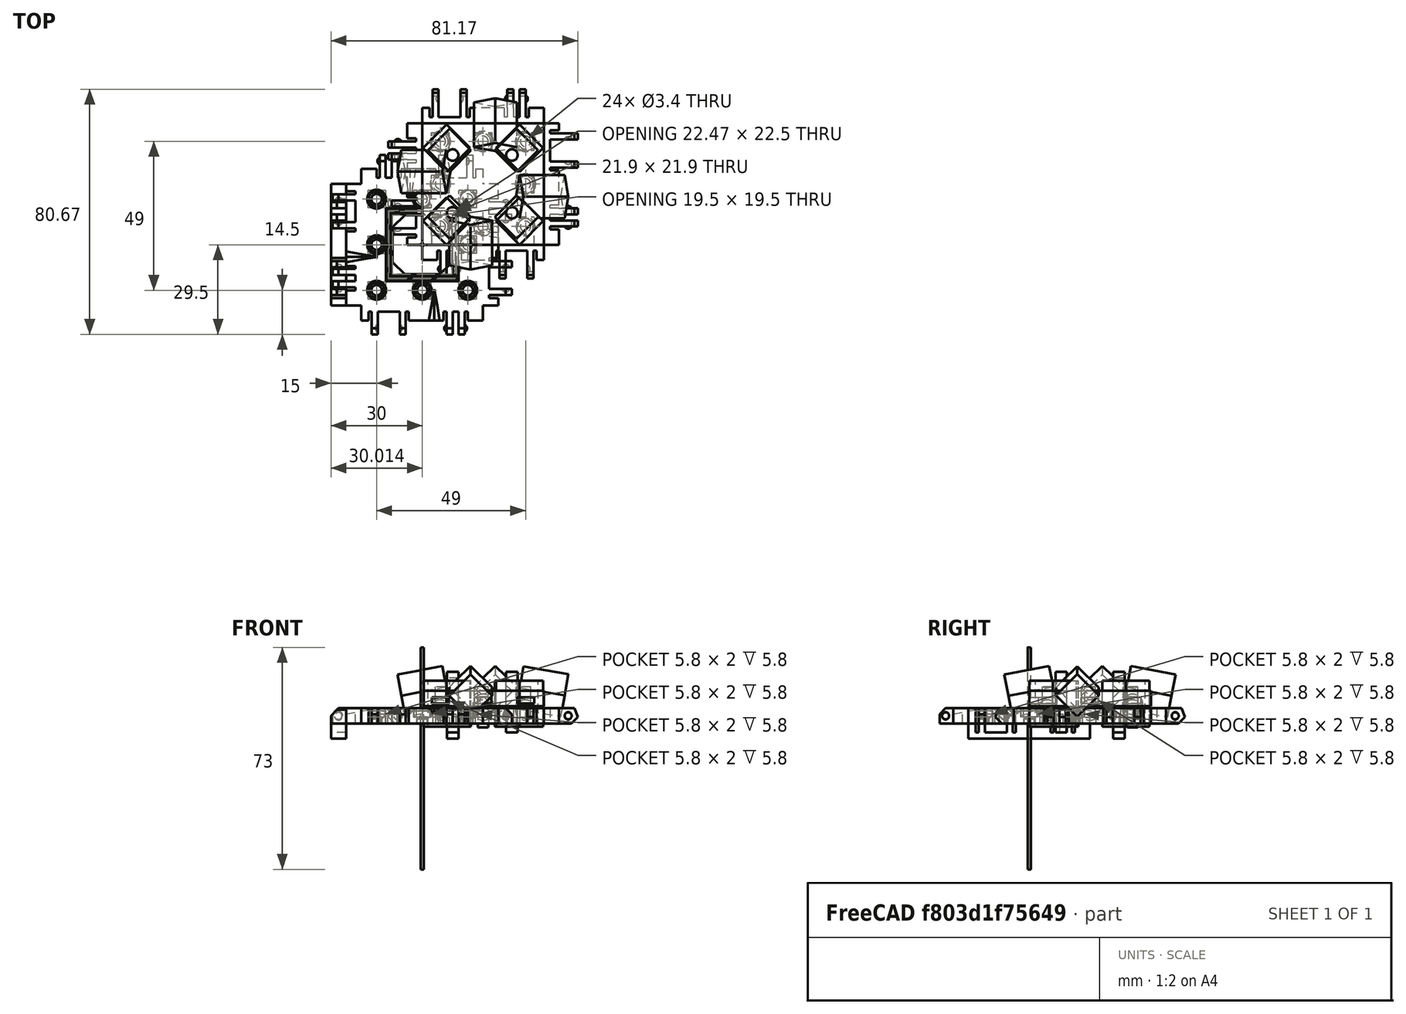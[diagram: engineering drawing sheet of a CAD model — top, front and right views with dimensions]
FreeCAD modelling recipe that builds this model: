
FCSTD DOCUMENT  (FreeCAD 0.17R13522 (Git))
Label: Robot Plates 1.2
License: All rights reserved
LicenseURL: http://en.wikipedia.org/wiki/All_rights_reserved
objects: Part::Box×265, Part::Cut×92, Part::Sphere×89, Part::MultiFuse×66, Part::Cylinder×42, Part::Fuse×30, Part::Chamfer×11, Drawing::FeatureViewAnnotation×10, App::DocumentObjectGroup×3, Part::Feature×3, Drawing::FeaturePage×2
note: 598 computed .brp shape members not serialized (recipe doc carries the construction recipe); baked Part::Feature solids carry a one-line shape summary decoded from their .brp

FEATURE [Part::Box] Box  label="Cube"
  AttacherType = Attacher::AttachEngine3D
  Height = 5
  Length = 40
  Placement = pos=(-20,-20,-2) rot=(0,0,1;0rad)
  Width = 40
FEATURE [Part::Sphere] Sphere003  label="Mag Hole 3"
  Angle1 = -90
  Angle2 = 90
  Angle3 = 360
  AttacherType = Attacher::AttachEngine3D
  Placement = pos=(-15,15,1.7) rot=(0,0,1;0rad)
  Radius = 2.83
FEATURE [Part::Sphere] Sphere005  label="Mag Hole 2"
  Angle1 = -90
  Angle2 = 90
  Angle3 = 360
  AttacherType = Attacher::AttachEngine3D
  Placement = pos=(15,0,1.7) rot=(0,0,1;0rad)
  Radius = 2.825
FEATURE [Part::Sphere] Sphere  label="Mag Hole"
  Angle1 = -90
  Angle2 = 90
  Angle3 = 360
  AttacherType = Attacher::AttachEngine3D
  Placement = pos=(-15,-15,1.7) rot=(0,0,1;0rad)
  Radius = 2.83
FEATURE [Part::MultiFuse] Fusion004  label="Ball Holes"
  Shapes = -> [Sphere,Sphere005,Sphere003]
FEATURE [Part::Cut] Cut003
  Base = -> Box
  Tool = -> Fusion004
FEATURE [Part::Box] Box001  label="Cube001"
  AttacherType = Attacher::AttachEngine3D
  Height = 7
  Length = 5
  Placement = pos=(-5,0,-2) rot=(0,0,1;0rad)
  Width = 40
FEATURE [Part::Box] Box002  label="Cube002"
  AttacherType = Attacher::AttachEngine3D
  Height = 7
  Length = 10
  Placement = pos=(-15,6,-2) rot=(0,0,1;0rad)
  Width = 2
FEATURE [Part::Box] Box003  label="Cube003"
  AttacherType = Attacher::AttachEngine3D
  Height = 7
  Length = 10
  Placement = pos=(-15,10,-2) rot=(0,0,1;0rad)
  Width = 2
FEATURE [Part::Box] Box004  label="Cube004"
  AttacherType = Attacher::AttachEngine3D
  Height = 7
  Length = 10
  Placement = pos=(-15,25.4,-2) rot=(0,0,1;0rad)
  Width = 2
FEATURE [Part::Box] Box005  label="Cube005"
  AttacherType = Attacher::AttachEngine3D
  Height = 7
  Length = 10
  Placement = pos=(-15,34.6,-2) rot=(0,0,1;0rad)
  Width = 2
FEATURE [Part::Sphere] Sphere008
  Angle1 = -90
  Angle2 = 90
  Angle3 = 360
  AttacherType = Attacher::AttachEngine3D
  Placement = pos=(-7.5,6.5,0.5) rot=(0,0,1;0rad)
  Radius = 1.25
FEATURE [Part::Box] Box006  label="Chamfer Cube"
  AttacherType = Attacher::AttachEngine3D
  Height = 10
  Length = 13
  Placement = pos=(-11.69,0,-1.19) rot=(0,-1,0;0.785398rad)
  Width = 40
FEATURE [Part::Sphere] Sphere009
  Angle1 = -90
  Angle2 = 90
  Angle3 = 360
  AttacherType = Attacher::AttachEngine3D
  Placement = pos=(-7.5,11.5,0.5) rot=(0,0,1;0rad)
  Radius = 1.25
FEATURE [Part::Sphere] Sphere010
  Angle1 = -90
  Angle2 = 90
  Angle3 = 360
  AttacherType = Attacher::AttachEngine3D
  Placement = pos=(-7.5,28,0.5) rot=(0,0,1;0rad)
  Radius = 1.5
FEATURE [Part::Sphere] Sphere011
  Angle1 = -90
  Angle2 = 90
  Angle3 = 360
  AttacherType = Attacher::AttachEngine3D
  Placement = pos=(-7.5,34,0.5) rot=(0,0,1;0rad)
  Radius = 1.5
FEATURE [Part::Box] Box007  label="Cube007"
  AttacherType = Attacher::AttachEngine3D
  Height = 7
  Length = 4
  Placement = pos=(-6,5,-2) rot=(0,0,1;0rad)
  Width = 1
FEATURE [Part::Box] Box008  label="Cube008"
  AttacherType = Attacher::AttachEngine3D
  Height = 7
  Length = 4
  Placement = pos=(-6,8,-2) rot=(0,0,1;0rad)
  Width = 2
FEATURE [Part::Box] Box009  label="Cube009"
  AttacherType = Attacher::AttachEngine3D
  Height = 7
  Length = 4
  Placement = pos=(-6,12,-2) rot=(0,0,1;0rad)
  Width = 1
FEATURE [Part::Box] Box010  label="Cube010"
  AttacherType = Attacher::AttachEngine3D
  Height = 7
  Length = 4
  Placement = pos=(-6,24.4,-2) rot=(0,0,1;0rad)
  Width = 1
FEATURE [Part::Box] Box011  label="Cube011"
  AttacherType = Attacher::AttachEngine3D
  Height = 7
  Length = 4
  Placement = pos=(-6,36.6,-2) rot=(0,0,1;0rad)
  Width = 1
FEATURE [Part::Box] Box012  label="Cube012"
  AttacherType = Attacher::AttachEngine3D
  Height = 7
  Length = 4
  Placement = pos=(-6,27.4,-2) rot=(0,0,1;0rad)
  Width = 7.2
FEATURE [Part::MultiFuse] Fusion003  label="Extra Holes for Clips"
  Shapes = -> [Box012,Box009,Box011,Box008,Box010,Box007]
FEATURE [Part::Box] Box013  label="Re-level Edge Clip Block"
  AttacherType = Attacher::AttachEngine3D
  Height = 10
  Length = 20
  Placement = pos=(-19,-2,3) rot=(0,0,1;0rad)
  Width = 44
FEATURE [Part::Box] Box014  label="Cube014"
  AttacherType = Attacher::AttachEngine3D
  Height = 7
  Length = 10
  Placement = pos=(-10,34.6,0) rot=(0,0,1;0rad)
  Width = 2
FEATURE [Part::Box] Box015  label="Cube015"
  AttacherType = Attacher::AttachEngine3D
  Height = 7
  Length = 5
  Width = 40
FEATURE [Part::Box] Box016  label="Cube016"
  AttacherType = Attacher::AttachEngine3D
  Height = 7
  Length = 10
  Placement = pos=(-10,25.4,0) rot=(0,0,1;0rad)
  Width = 2
FEATURE [Part::Box] Box017  label="Cube017"
  AttacherType = Attacher::AttachEngine3D
  Height = 7
  Length = 10
  Placement = pos=(-10,10,0) rot=(0,0,1;0rad)
  Width = 2
FEATURE [Part::Box] Box018  label="Cube018"
  AttacherType = Attacher::AttachEngine3D
  Height = 7
  Length = 10
  Placement = pos=(-10,6,0) rot=(0,0,1;0rad)
  Width = 2
FEATURE [Part::Sphere] Sphere012
  Angle1 = -90
  Angle2 = 90
  Angle3 = 360
  AttacherType = Attacher::AttachEngine3D
  Placement = pos=(-3,6.5,2.5) rot=(0,0,1;0rad)
  Radius = 1.25
FEATURE [Part::Box] Box019  label="Cube019"
  AttacherType = Attacher::AttachEngine3D
  Height = 10
  Length = 13
  Placement = pos=(-10.19,0,-1.19) rot=(0,-1,0;0.785398rad)
  Width = 40
FEATURE [Part::Sphere] Sphere013
  Angle1 = -90
  Angle2 = 90
  Angle3 = 360
  AttacherType = Attacher::AttachEngine3D
  Placement = pos=(-3,11.5,2.5) rot=(0,0,1;0rad)
  Radius = 1.25
FEATURE [Part::Sphere] Sphere014
  Angle1 = -90
  Angle2 = 90
  Angle3 = 360
  AttacherType = Attacher::AttachEngine3D
  Placement = pos=(-3,28,2.5) rot=(0,0,1;0rad)
  Radius = 1.5
FEATURE [Part::Sphere] Sphere015
  Angle1 = -90
  Angle2 = 90
  Angle3 = 360
  AttacherType = Attacher::AttachEngine3D
  Placement = pos=(-3,34,2.5) rot=(0,0,1;0rad)
  Radius = 1.5
FEATURE [Part::MultiFuse] Fusion005
  Shapes = -> [Box015,Box018,Box017,Box016,Box014]
FEATURE [Part::Cut] Cut005
  Base = -> Fusion005
  Tool = -> Box019
FEATURE [Part::MultiFuse] Fusion006
  Shapes = -> [Sphere012,Sphere013,Cut005]
FEATURE [Part::MultiFuse] Fusion007
  Shapes = -> [Sphere015,Sphere014]
FEATURE [Part::Cut] Cut006
  Base = -> Fusion006
  Tool = -> Fusion007
FEATURE [Part::Chamfer] Chamfer002
  Base = -> Cut006
  Edges = 4 edges r=4: [Edge31,Edge37,Edge43,Edge46]
FEATURE [Part::Box] Box020  label="Cube020"
  AttacherType = Attacher::AttachEngine3D
  Height = 7
  Length = 4
  Placement = pos=(-1,5,0) rot=(0,0,1;0rad)
  Width = 1
FEATURE [Part::Box] Box021  label="Cube021"
  AttacherType = Attacher::AttachEngine3D
  Height = 7
  Length = 4
  Placement = pos=(-1,8,0) rot=(0,0,1;0rad)
  Width = 2
FEATURE [Part::Box] Box022  label="Cube022"
  AttacherType = Attacher::AttachEngine3D
  Height = 7
  Length = 4
  Placement = pos=(-1,12,0) rot=(0,0,1;0rad)
  Width = 1
FEATURE [Part::Box] Box023  label="Cube023"
  AttacherType = Attacher::AttachEngine3D
  Height = 7
  Length = 4
  Placement = pos=(-1,24.4,0) rot=(0,0,1;0rad)
  Width = 1
FEATURE [Part::Box] Box024  label="Cube024"
  AttacherType = Attacher::AttachEngine3D
  Height = 7
  Length = 4
  Placement = pos=(-1,36.6,0) rot=(0,0,1;0rad)
  Width = 1
FEATURE [Part::Box] Box025  label="Cube025"
  AttacherType = Attacher::AttachEngine3D
  Height = 7
  Length = 4
  Placement = pos=(-1,27.4,0) rot=(0,0,1;0rad)
  Width = 7.2
FEATURE [Part::MultiFuse] Fusion008
  Shapes = -> [Box025,Box022,Box024,Box021,Box023,Box020]
FEATURE [Part::Cut] Cut007
  Base = -> Chamfer002
  Placement = pos=(-5,40,3) rot=(1,0,0;3.14159rad)
  Tool = -> Fusion008
FEATURE [Part::Box] Box026  label="Cube026"
  AttacherType = Attacher::AttachEngine3D
  Height = 10
  Length = 12
  Placement = pos=(-11,-2,-12) rot=(0,0,1;0rad)
  Width = 44
FEATURE [Part::Cut] Cut008
  Base = -> Cut007
  Placement = pos=(40,0,0) rot=(0,0,1;1.5708rad)
  Tool = -> Box026
FEATURE [Part::Box] Box027  label="Cube027"
  AttacherType = Attacher::AttachEngine3D
  Height = 7
  Length = 4
  Placement = pos=(-1,12,0) rot=(0,0,1;0rad)
  Width = 1
FEATURE [Part::Box] Box028  label="Cube028"
  AttacherType = Attacher::AttachEngine3D
  Height = 10
  Length = 13
  Placement = pos=(-10.19,0,-1.19) rot=(0,-1,0;0.785398rad)
  Width = 40
FEATURE [Part::Box] Box029  label="Cube029"
  AttacherType = Attacher::AttachEngine3D
  Height = 7
  Length = 4
  Placement = pos=(-1,27.4,0) rot=(0,0,1;0rad)
  Width = 7.2
FEATURE [Part::Box] Box030  label="Cube030"
  AttacherType = Attacher::AttachEngine3D
  Height = 7
  Length = 4
  Placement = pos=(-1,5,0) rot=(0,0,1;0rad)
  Width = 1
FEATURE [Part::Box] Box031  label="Cube031"
  AttacherType = Attacher::AttachEngine3D
  Height = 7
  Length = 10
  Placement = pos=(-10,6,0) rot=(0,0,1;0rad)
  Width = 2
FEATURE [Part::Box] Box032  label="Cube032"
  AttacherType = Attacher::AttachEngine3D
  Height = 10
  Length = 12
  Placement = pos=(-11,-2,-12) rot=(0,0,1;0rad)
  Width = 44
FEATURE [Part::Sphere] Sphere016
  Angle1 = -90
  Angle2 = 90
  Angle3 = 360
  AttacherType = Attacher::AttachEngine3D
  Placement = pos=(-3,6.5,2.5) rot=(0,0,1;0rad)
  Radius = 1.25
FEATURE [Part::Box] Box033  label="Cube033"
  AttacherType = Attacher::AttachEngine3D
  Height = 7
  Length = 10
  Placement = pos=(-10,25.4,0) rot=(0,0,1;0rad)
  Width = 2
FEATURE [Part::Box] Box034  label="Cube034"
  AttacherType = Attacher::AttachEngine3D
  Height = 7
  Length = 10
  Placement = pos=(-10,10,0) rot=(0,0,1;0rad)
  Width = 2
FEATURE [Part::Sphere] Sphere017
  Angle1 = -90
  Angle2 = 90
  Angle3 = 360
  AttacherType = Attacher::AttachEngine3D
  Placement = pos=(-3,28,2.5) rot=(0,0,1;0rad)
  Radius = 1.5
FEATURE [Part::Sphere] Sphere018
  Angle1 = -90
  Angle2 = 90
  Angle3 = 360
  AttacherType = Attacher::AttachEngine3D
  Placement = pos=(-3,11.5,2.5) rot=(0,0,1;0rad)
  Radius = 1.25
FEATURE [Part::Box] Box035  label="Cube035"
  AttacherType = Attacher::AttachEngine3D
  Height = 7
  Length = 4
  Placement = pos=(-1,36.6,0) rot=(0,0,1;0rad)
  Width = 1
FEATURE [Part::Sphere] Sphere019
  Angle1 = -90
  Angle2 = 90
  Angle3 = 360
  AttacherType = Attacher::AttachEngine3D
  Placement = pos=(-3,34,2.5) rot=(0,0,1;0rad)
  Radius = 1.5
FEATURE [Part::MultiFuse] Fusion011
  Shapes = -> [Sphere019,Sphere017]
FEATURE [Part::Box] Box036  label="Cube036"
  AttacherType = Attacher::AttachEngine3D
  Height = 7
  Length = 4
  Placement = pos=(-1,8,0) rot=(0,0,1;0rad)
  Width = 2
FEATURE [Part::Box] Box037  label="Cube037"
  AttacherType = Attacher::AttachEngine3D
  Height = 7
  Length = 10
  Placement = pos=(-10,34.6,0) rot=(0,0,1;0rad)
  Width = 2
FEATURE [Part::Box] Box038  label="Cube038"
  AttacherType = Attacher::AttachEngine3D
  Height = 7
  Length = 4
  Placement = pos=(-1,24.4,0) rot=(0,0,1;0rad)
  Width = 1
FEATURE [Part::MultiFuse] Fusion009
  Shapes = -> [Box029,Box027,Box035,Box036,Box038,Box030]
FEATURE [Part::Box] Box039  label="Cube039"
  AttacherType = Attacher::AttachEngine3D
  Height = 7
  Length = 5
  Width = 40
FEATURE [Part::MultiFuse] Fusion012
  Shapes = -> [Box039,Box031,Box034,Box033,Box037]
FEATURE [Part::Cut] Cut011
  Base = -> Fusion012
  Tool = -> Box028
FEATURE [Part::MultiFuse] Fusion010
  Shapes = -> [Sphere016,Sphere018,Cut011]
FEATURE [Part::Cut] Cut012
  Base = -> Fusion010
  Tool = -> Fusion011
FEATURE [Part::Chamfer] Chamfer003
  Base = -> Cut012
  Edges = 4 edges r=4: [Edge31,Edge37,Edge43,Edge46]
FEATURE [Part::Cut] Cut010
  Base = -> Chamfer003
  Placement = pos=(-5,40,3) rot=(1,0,0;3.14159rad)
  Tool = -> Fusion009
FEATURE [Part::Cut] Cut009
  Base = -> Cut010
  Placement = pos=(40,40,0) rot=(0,0,1;3.14159rad)
  Tool = -> Box032
FEATURE [Part::Sphere] Sphere020
  Angle1 = -90
  Angle2 = 90
  Angle3 = 360
  AttacherType = Attacher::AttachEngine3D
  Placement = pos=(-3,11.5,2.5) rot=(0,0,1;0rad)
  Radius = 1.25
FEATURE [Part::Box] Box040  label="Cube040"
  AttacherType = Attacher::AttachEngine3D
  Height = 7
  Length = 10
  Placement = pos=(-10,6,0) rot=(0,0,1;0rad)
  Width = 2
FEATURE [Part::Box] Box041  label="Cube041"
  AttacherType = Attacher::AttachEngine3D
  Height = 7
  Length = 4
  Placement = pos=(-1,8,0) rot=(0,0,1;0rad)
  Width = 2
FEATURE [Part::Box] Box042  label="Cube042"
  AttacherType = Attacher::AttachEngine3D
  Height = 7
  Length = 10
  Placement = pos=(-10,10,0) rot=(0,0,1;0rad)
  Width = 2
FEATURE [Part::Box] Box043  label="Cube043"
  AttacherType = Attacher::AttachEngine3D
  Height = 10
  Length = 12
  Placement = pos=(-11,-2,-12) rot=(0,0,1;0rad)
  Width = 44
FEATURE [Part::Box] Box044  label="Cube044"
  AttacherType = Attacher::AttachEngine3D
  Height = 7
  Length = 4
  Placement = pos=(-1,5,0) rot=(0,0,1;0rad)
  Width = 1
FEATURE [Part::Sphere] Sphere021
  Angle1 = -90
  Angle2 = 90
  Angle3 = 360
  AttacherType = Attacher::AttachEngine3D
  Placement = pos=(-3,28,2.5) rot=(0,0,1;0rad)
  Radius = 1.5
FEATURE [Part::Sphere] Sphere022
  Angle1 = -90
  Angle2 = 90
  Angle3 = 360
  AttacherType = Attacher::AttachEngine3D
  Placement = pos=(-3,6.5,2.5) rot=(0,0,1;0rad)
  Radius = 1.25
FEATURE [Part::Sphere] Sphere023
  Angle1 = -90
  Angle2 = 90
  Angle3 = 360
  AttacherType = Attacher::AttachEngine3D
  Placement = pos=(-3,34,2.5) rot=(0,0,1;0rad)
  Radius = 1.5
FEATURE [Part::Box] Box045  label="Cube045"
  AttacherType = Attacher::AttachEngine3D
  Height = 7
  Length = 4
  Placement = pos=(-1,12,0) rot=(0,0,1;0rad)
  Width = 1
FEATURE [Part::Box] Box046  label="Cube046"
  AttacherType = Attacher::AttachEngine3D
  Height = 7
  Length = 5
  Width = 40
FEATURE [Part::Box] Box047  label="Cube047"
  AttacherType = Attacher::AttachEngine3D
  Height = 7
  Length = 4
  Placement = pos=(-1,36.6,0) rot=(0,0,1;0rad)
  Width = 1
FEATURE [Part::Box] Box048  label="Cube048"
  AttacherType = Attacher::AttachEngine3D
  Height = 7
  Length = 4
  Placement = pos=(-1,24.4,0) rot=(0,0,1;0rad)
  Width = 1
FEATURE [Part::Box] Box049  label="Cube049"
  AttacherType = Attacher::AttachEngine3D
  Height = 7
  Length = 10
  Placement = pos=(-10,25.4,0) rot=(0,0,1;0rad)
  Width = 2
FEATURE [Part::Box] Box050  label="Cube050"
  AttacherType = Attacher::AttachEngine3D
  Height = 10
  Length = 13
  Placement = pos=(-10.19,0,-1.19) rot=(0,-1,0;0.785398rad)
  Width = 40
FEATURE [Part::Box] Box051  label="Cube051"
  AttacherType = Attacher::AttachEngine3D
  Height = 7
  Length = 10
  Placement = pos=(-10,34.6,0) rot=(0,0,1;0rad)
  Width = 2
FEATURE [Part::MultiFuse] Fusion015
  Shapes = -> [Box046,Box040,Box042,Box049,Box051]
FEATURE [Part::Cut] Cut013
  Base = -> Fusion015
  Tool = -> Box050
FEATURE [Part::MultiFuse] Fusion013
  Shapes = -> [Sphere022,Sphere020,Cut013]
FEATURE [Part::MultiFuse] Fusion016
  Shapes = -> [Sphere023,Sphere021]
FEATURE [Part::Cut] Cut014
  Base = -> Fusion013
  Tool = -> Fusion016
FEATURE [Part::Chamfer] Chamfer004
  Base = -> Cut014
  Edges = 4 edges r=4: [Edge31,Edge37,Edge43,Edge46]
FEATURE [Part::Box] Box052  label="Cube052"
  AttacherType = Attacher::AttachEngine3D
  Height = 7
  Length = 4
  Placement = pos=(-1,27.4,0) rot=(0,0,1;0rad)
  Width = 7.2
FEATURE [Part::MultiFuse] Fusion014
  Shapes = -> [Box052,Box045,Box047,Box041,Box048,Box044]
FEATURE [Part::Cut] Cut016
  Base = -> Chamfer004
  Placement = pos=(-5,40,3) rot=(1,0,0;3.14159rad)
  Tool = -> Fusion014
FEATURE [Part::Cut] Cut015
  Base = -> Cut016
  Placement = pos=(0,40,0) rot=(0,0,-1;1.5708rad)
  Tool = -> Box043
FEATURE [Part::Box] Box054  label="Cube054"
  AttacherType = Attacher::AttachEngine3D
  Height = 15
  Length = 10
  Placement = pos=(9,2,-3) rot=(0,0,1;0.785398rad)
  Width = 10
FEATURE [Part::Box] Box055  label="Cube055"
  AttacherType = Attacher::AttachEngine3D
  Height = 15
  Length = 10
  Placement = pos=(31,24,-3) rot=(0,0,1;0.785398rad)
  Width = 10
FEATURE [Part::Box] Box056  label="Cube056"
  AttacherType = Attacher::AttachEngine3D
  Height = 15
  Length = 10
  Placement = pos=(31,2,-3) rot=(0,0,1;0.785398rad)
  Width = 10
FEATURE [Part::Box] Box057  label="Cube057"
  AttacherType = Attacher::AttachEngine3D
  Height = 15
  Length = 10
  Placement = pos=(9,24,-3) rot=(0,0,1;0.785398rad)
  Width = 10
FEATURE [Part::MultiFuse] Fusion017
  Shapes = -> [Box054,Box057,Box056,Box055]
FEATURE [Part::Box] Box058  label="Cube058"
  AttacherType = Attacher::AttachEngine3D
  Height = 5
  Length = 40
  Placement = pos=(0,0,3.7) rot=(0,0,1;0rad)
  Width = 40
FEATURE [Part::Box] Box059  label="Square Nut Hole 008"
  AttacherType = Attacher::AttachEngine3D
  Height = 2
  Length = 5.6
  Placement = pos=(17.2,31.2,4.6) rot=(0,0,1;0rad)
  Width = 5.6
FEATURE [Part::Box] Box060  label="Square Nut Hole 009"
  AttacherType = Attacher::AttachEngine3D
  Height = 2
  Length = 5.6
  Placement = pos=(17.2,-0.85,4.6) rot=(0,0,1;0rad)
  Width = 10
FEATURE [Part::Box] Box061  label="Square Nut Hole 010"
  AttacherType = Attacher::AttachEngine3D
  Height = 2
  Length = 5.6
  Placement = pos=(31.2,-0.85,4.6) rot=(0,0,1;0rad)
  Width = 10
FEATURE [Part::Box] Box062  label="Square Nut Hole 011"
  AttacherType = Attacher::AttachEngine3D
  Height = 2
  Length = 5.4
  Placement = pos=(31.3,17.3,4.6) rot=(0,0,1;0rad)
  Width = 5.4
FEATURE [Part::Box] Box063  label="Square Nut Hole 012"
  AttacherType = Attacher::AttachEngine3D
  Height = 2
  Length = 5.7
  Placement = pos=(3.15,31.15,4.6) rot=(0,0,1;0rad)
  Width = 5.7
FEATURE [Part::Box] Box064  label="Square Nut Hole 013"
  AttacherType = Attacher::AttachEngine3D
  Height = 2
  Length = 5.5
  Placement = pos=(31.25,31.25,4.6) rot=(0,0,1;0rad)
  Width = 5.5
FEATURE [Part::Box] Box065  label="Square Nut Hole 014"
  AttacherType = Attacher::AttachEngine3D
  Height = 2
  Length = 5.8
  Placement = pos=(3.1,17.1,4.6) rot=(0,0,1;0rad)
  Width = 5.8
FEATURE [Part::Box] Box066  label="Square Nut Hole 015"
  AttacherType = Attacher::AttachEngine3D
  Height = 2
  Length = 5.6
  Placement = pos=(3.2,-0.85,4.6) rot=(0,0,1;0rad)
  Width = 10
FEATURE [Part::Sphere] Sphere006  label="Nut Clearence1"
  Angle1 = -90
  Angle2 = 90
  Angle3 = 360
  AttacherType = Attacher::AttachEngine3D
  Placement = pos=(6,6,2.4) rot=(0,0,1;0rad)
  Radius = 3.35
FEATURE [Part::Sphere] Sphere024
  Angle1 = -90
  Angle2 = 90
  Angle3 = 360
  AttacherType = Attacher::AttachEngine3D
  Placement = pos=(6,34,2.4) rot=(0,0,1;0rad)
  Radius = 3.35
FEATURE [Part::Sphere] Sphere007
  Angle1 = -90
  Angle2 = 90
  Angle3 = 360
  AttacherType = Attacher::AttachEngine3D
  Placement = pos=(34,20,2.4) rot=(0,0,1;0rad)
  Radius = 3.35
FEATURE [Part::Sphere] Sphere001
  Angle1 = -90
  Angle2 = 90
  Angle3 = 360
  AttacherType = Attacher::AttachEngine3D
  Placement = pos=(34,6,2.4) rot=(0,0,1;0rad)
  Radius = 3.35
FEATURE [Part::Sphere] Sphere025
  Angle1 = -90
  Angle2 = 90
  Angle3 = 360
  AttacherType = Attacher::AttachEngine3D
  Placement = pos=(20,6,2.4) rot=(0,0,1;0rad)
  Radius = 3.35
FEATURE [Part::Sphere] Sphere026
  Angle1 = -90
  Angle2 = 90
  Angle3 = 360
  AttacherType = Attacher::AttachEngine3D
  Placement = pos=(20,34,2.4) rot=(0,0,1;0rad)
  Radius = 3.35
FEATURE [Part::Sphere] Sphere004
  Angle1 = -90
  Angle2 = 90
  Angle3 = 360
  AttacherType = Attacher::AttachEngine3D
  Placement = pos=(6,20,2.4) rot=(0,0,1;0rad)
  Radius = 3.35
FEATURE [Part::Sphere] Sphere002
  Angle1 = -90
  Angle2 = 90
  Angle3 = 360
  AttacherType = Attacher::AttachEngine3D
  Placement = pos=(34,34,2.4) rot=(0,0,1;0rad)
  Radius = 3.35
FEATURE [Part::Cylinder] Cylinder
  Angle = 360
  AttacherType = Attacher::AttachEngine3D
  Height = 10
  Placement = pos=(6,6,0) rot=(0,0,1;0rad)
  Radius = 1.7
FEATURE [Part::Cylinder] Cylinder002
  Angle = 360
  AttacherType = Attacher::AttachEngine3D
  Height = 10
  Placement = pos=(34,6,0) rot=(0,0,1;0rad)
  Radius = 1.7
FEATURE [Part::Cylinder] Cylinder001
  Angle = 360
  AttacherType = Attacher::AttachEngine3D
  Height = 10
  Placement = pos=(20,6,0) rot=(0,0,1;0rad)
  Radius = 1.7
FEATURE [Part::Cylinder] Cylinder003
  Angle = 360
  AttacherType = Attacher::AttachEngine3D
  Height = 10
  Placement = pos=(34,34,0) rot=(0,0,1;0rad)
  Radius = 1.7
FEATURE [Part::Cylinder] Cylinder004
  Angle = 360
  AttacherType = Attacher::AttachEngine3D
  Height = 10
  Placement = pos=(20,34,0) rot=(0,0,1;0rad)
  Radius = 1.7
FEATURE [Part::Cylinder] Cylinder005
  Angle = 360
  AttacherType = Attacher::AttachEngine3D
  Height = 10
  Placement = pos=(6,34,0) rot=(0,0,1;0rad)
  Radius = 1.7
FEATURE [Part::Cylinder] Cylinder006
  Angle = 360
  AttacherType = Attacher::AttachEngine3D
  Height = 10
  Placement = pos=(6,20,0) rot=(0,0,1;0rad)
  Radius = 1.7
FEATURE [Part::Cylinder] Cylinder007
  Angle = 360
  AttacherType = Attacher::AttachEngine3D
  Height = 10
  Placement = pos=(34,20,0) rot=(0,0,1;0rad)
  Radius = 1.7
FEATURE [Part::MultiFuse] Fusion018
  Shapes = -> [Cylinder,Cylinder004,Cylinder007,Cylinder005,Cylinder006,Cylinder001,Cylinder002,Cylinder003]
FEATURE [Part::MultiFuse] Fusion019
  Shapes = -> [Sphere007,Sphere024,Sphere006,Sphere025,Sphere001,Sphere026,Sphere004,Sphere002]
FEATURE [Part::MultiFuse] Fusion020
  Shapes = -> [Box061,Box065,Box062,Box063,Box064,Box066,Box059,Box060]
FEATURE [Part::Cut] Cut017
  Base = -> Box058
  Tool = -> Fusion020
FEATURE [Part::Cut] Cut019
  Base = -> Cut017
  Tool = -> Fusion019
FEATURE [Part::Cut] Cut018
  Base = -> Cut019
  Tool = -> Fusion018
FEATURE [Part::Cylinder] Cylinder008
  Angle = 360
  AttacherType = Attacher::AttachEngine3D
  Height = 20
  Placement = pos=(10,10.5,-5) rot=(0,0,1;0rad)
  Radius = 1.9
FEATURE [Part::Cylinder] Cylinder009
  Angle = 360
  AttacherType = Attacher::AttachEngine3D
  Height = 20
  Placement = pos=(29.5,10.5,-5) rot=(0,0,1;0rad)
  Radius = 1.9
FEATURE [Part::Cylinder] Cylinder010
  Angle = 360
  AttacherType = Attacher::AttachEngine3D
  Height = 20
  Placement = pos=(29.5,29.5,-5) rot=(0,0,1;0rad)
  Radius = 1.9
FEATURE [Part::Cylinder] Cylinder011
  Angle = 360
  AttacherType = Attacher::AttachEngine3D
  Height = 20
  Placement = pos=(10,29.5,-7) rot=(0,0,1;0rad)
  Radius = 1.9
FEATURE [Part::MultiFuse] Fusion021  label="M2 Screw holes"
  Shapes = -> [Cylinder008,Cylinder009,Cylinder011,Cylinder010]
FEATURE [Part::Box] Box067  label="Square Nut Hole 016"
  AttacherType = Attacher::AttachEngine3D
  Height = 2
  Length = 5.8
  Placement = pos=(31.1,17.1,4.6) rot=(0,0,1;0rad)
  Width = 5.8
FEATURE [Part::Box] Box068  label="Square Nut Hole 017"
  AttacherType = Attacher::AttachEngine3D
  Height = 2
  Length = 5.8
  Placement = pos=(17.1,36.9,2.1) rot=(1,0,0;3.14159rad)
  Width = 5.8
FEATURE [Part::Box] Box069  label="Square Nut Hole 018"
  AttacherType = Attacher::AttachEngine3D
  Height = 2
  Length = 5.8
  Placement = pos=(-2.9,2.9,2.1) rot=(1,0,0;3.14159rad)
  Width = 5.8
FEATURE [Part::Box] Box070  label="Square Nut Hole 019"
  AttacherType = Attacher::AttachEngine3D
  Height = 2
  Length = 5.8
  Placement = pos=(3.1,3.1,4.6) rot=(0,0,1;0rad)
  Width = 5.8
FEATURE [Part::Box] Box071  label="Square Nut Hole 020"
  AttacherType = Attacher::AttachEngine3D
  Height = 2
  Length = 5.8
  Placement = pos=(3.1,31.1,4.6) rot=(0,0,1;0rad)
  Width = 5.8
FEATURE [Part::Box] Box072  label="Square Nut Hole 021"
  AttacherType = Attacher::AttachEngine3D
  Height = 2
  Length = 5.8
  Placement = pos=(17.1,31.1,4.6) rot=(0,0,1;0rad)
  Width = 5.8
FEATURE [Part::Box] Box073  label="Square Nut Hole 022"
  AttacherType = Attacher::AttachEngine3D
  Height = 2
  Length = 5.8
  Placement = pos=(31.1,31.1,4.6) rot=(0,0,1;0rad)
  Width = 5.8
FEATURE [Part::Box] Box074  label="Square Nut Hole 023"
  AttacherType = Attacher::AttachEngine3D
  Height = 2
  Length = 5.8
  Placement = pos=(3.1,17.1,4.6) rot=(0,0,1;0rad)
  Width = 5.8
FEATURE [Part::Cylinder] Cylinder012
  Angle = 360
  AttacherType = Attacher::AttachEngine3D
  Height = 10
  Placement = pos=(6,6,0) rot=(0,0,1;0rad)
  Radius = 1.7
FEATURE [Part::Cylinder] Cylinder013
  Angle = 360
  AttacherType = Attacher::AttachEngine3D
  Height = 10
  Placement = pos=(34,34,0) rot=(0,0,1;0rad)
  Radius = 1.7
FEATURE [Part::Cylinder] Cylinder014
  Angle = 360
  AttacherType = Attacher::AttachEngine3D
  Height = 10
  Placement = pos=(20,34,0) rot=(0,0,1;0rad)
  Radius = 1.7
FEATURE [Part::Cylinder] Cylinder015
  Angle = 360
  AttacherType = Attacher::AttachEngine3D
  Height = 10
  Placement = pos=(6,34,0) rot=(0,0,1;0rad)
  Radius = 1.7
FEATURE [Part::Cylinder] Cylinder016
  Angle = 360
  AttacherType = Attacher::AttachEngine3D
  Height = 10
  Placement = pos=(6,20,0) rot=(0,0,1;0rad)
  Radius = 1.7
FEATURE [Part::Cylinder] Cylinder017
  Angle = 360
  AttacherType = Attacher::AttachEngine3D
  Height = 10
  Placement = pos=(34,20,0) rot=(0,0,1;0rad)
  Radius = 1.7
FEATURE [Part::Cylinder] Cylinder018
  Angle = 360
  AttacherType = Attacher::AttachEngine3D
  Height = 10
  Placement = pos=(0,0,6.7) rot=(1,0,0;3.14159rad)
  Radius = 1.7
FEATURE [Part::Cylinder] Cylinder019
  Angle = 360
  AttacherType = Attacher::AttachEngine3D
  Height = 10
  Placement = pos=(20,34,6.7) rot=(1,0,0;3.14159rad)
  Radius = 1.7
FEATURE [Part::Box] Box075  label="Cube059"
  AttacherType = Attacher::AttachEngine3D
  Height = 5
  Length = 40
  Placement = pos=(-20,-20,-2) rot=(0,0,1;0rad)
  Width = 40
FEATURE [Part::Sphere] Sphere027
  Angle1 = -90
  Angle2 = 90
  Angle3 = 360
  AttacherType = Attacher::AttachEngine3D
  Placement = pos=(34,20,2.4) rot=(0,0,1;0rad)
  Radius = 3.35
FEATURE [Part::Sphere] Sphere028  label="Nut Clearence002"
  Angle1 = -90
  Angle2 = 90
  Angle3 = 360
  AttacherType = Attacher::AttachEngine3D
  Placement = pos=(6,6,2.4) rot=(0,0,1;0rad)
  Radius = 3.35
FEATURE [Part::Sphere] Sphere029
  Angle1 = -90
  Angle2 = 90
  Angle3 = 360
  AttacherType = Attacher::AttachEngine3D
  Placement = pos=(34,34,2.4) rot=(0,0,1;0rad)
  Radius = 3.35
FEATURE [Part::Sphere] Sphere030
  Angle1 = -90
  Angle2 = 90
  Angle3 = 360
  AttacherType = Attacher::AttachEngine3D
  Placement = pos=(0,0,4.3) rot=(1,0,0;3.14159rad)
  Radius = 3.35
FEATURE [Part::Sphere] Sphere031
  Angle1 = -90
  Angle2 = 90
  Angle3 = 360
  AttacherType = Attacher::AttachEngine3D
  Placement = pos=(20,34,4.3) rot=(1,0,0;3.14159rad)
  Radius = 3.35
FEATURE [Part::Sphere] Sphere032
  Angle1 = -90
  Angle2 = 90
  Angle3 = 360
  AttacherType = Attacher::AttachEngine3D
  Placement = pos=(6,34,2.4) rot=(0,0,1;0rad)
  Radius = 3.35
FEATURE [Part::Sphere] Sphere033
  Angle1 = -90
  Angle2 = 90
  Angle3 = 360
  AttacherType = Attacher::AttachEngine3D
  Placement = pos=(6,20,2.4) rot=(0,0,1;0rad)
  Radius = 3.35
FEATURE [Part::Sphere] Sphere034
  Angle1 = -90
  Angle2 = 90
  Angle3 = 360
  AttacherType = Attacher::AttachEngine3D
  Placement = pos=(20,34,2.4) rot=(0,0,1;0rad)
  Radius = 3.35
FEATURE [Part::Box] Box076  label="Cube060"
  AttacherType = Attacher::AttachEngine3D
  Height = 15
  Length = 19.5
  Placement = pos=(-9.75,-9.75,-3) rot=(0,0,1;0rad)
  Width = 19.5
FEATURE [Part::Box] Box077  label="Cube061"
  AttacherType = Attacher::AttachEngine3D
  Height = 15
  Length = 11
  Placement = pos=(8,24,-3) rot=(0,0,1;0.785398rad)
  Width = 11
FEATURE [Part::Box] Box078  label="Cube062"
  AttacherType = Attacher::AttachEngine3D
  Height = 15
  Length = 11
  Placement = pos=(8,0,-3) rot=(0,0,1;0.785398rad)
  Width = 11
FEATURE [Part::Box] Box079  label="Cube063"
  AttacherType = Attacher::AttachEngine3D
  Height = 15
  Length = 11
  Placement = pos=(32,0,-3) rot=(0,0,1;0.785398rad)
  Width = 11
FEATURE [Part::Box] Box080  label="Cube064"
  AttacherType = Attacher::AttachEngine3D
  Height = 15
  Length = 11
  Placement = pos=(32,24,-3) rot=(0,0,1;0.785398rad)
  Width = 11
FEATURE [Part::MultiFuse] Fusion022
  Shapes = -> [Box078,Box077,Box079,Box080]
FEATURE [Part::Cylinder] Cylinder020
  Angle = 360
  AttacherType = Attacher::AttachEngine3D
  Height = 20
  Placement = pos=(29.5,10.5,-5) rot=(0,0,1;0rad)
  Radius = 1.9
FEATURE [Part::Cylinder] Cylinder021
  Angle = 360
  AttacherType = Attacher::AttachEngine3D
  Height = 20
  Placement = pos=(10,29.5,-7) rot=(0,0,1;0rad)
  Radius = 1.9
FEATURE [Part::Cylinder] Cylinder022
  Angle = 360
  AttacherType = Attacher::AttachEngine3D
  Height = 20
  Placement = pos=(10,10.5,-5) rot=(0,0,1;0rad)
  Radius = 1.9
FEATURE [Part::Cylinder] Cylinder023
  Angle = 360
  AttacherType = Attacher::AttachEngine3D
  Height = 20
  Placement = pos=(29.5,29.5,-5) rot=(0,0,1;0rad)
  Radius = 1.9
FEATURE [Part::MultiFuse] Fusion023  label="M2 Screw holes001"
  Shapes = -> [Cylinder022,Cylinder020,Cylinder021,Cylinder023]
FEATURE [App::DocumentObjectGroup] Group  label="Cubes"
  Group = -> [Fusion017,Fusion022]
FEATURE [Part::Box] Box083  label="Cube067"
  AttacherType = Attacher::AttachEngine3D
  Height = 10
  Length = 24
  Placement = pos=(-12,-12,2.1) rot=(0,0,1;0rad)
  Width = 24
FEATURE [Part::Box] Box084  label="Cube068"
  AttacherType = Attacher::AttachEngine3D
  Height = 14
  Length = 20
  Placement = pos=(-10,-10,0) rot=(0,0,1;0rad)
  Width = 20
FEATURE [Part::Cut] Cut020
  Base = -> Box083
  Tool = -> Box084
FEATURE [Part::Chamfer] Chamfer007  label="Glue Channel Ball"
  Base = -> Cut020
  Edges = 8 edges r=0.95: [Edge4,Edge5,Edge14,Edge16,Edge17,Edge18,Edge19,Edge20]
FEATURE [Part::Chamfer] Chamfer008  label="Octogon Ball"
  Base = -> Box076
  Edges = 4 edges r=4: [Edge1,Edge3,Edge5,Edge7]
FEATURE [Part::Box] Box085  label="Cube069"
  AttacherType = Attacher::AttachEngine3D
  Height = 15
  Length = 19.5
  Placement = pos=(-9.75,-9.75,-14) rot=(0,0,1;0rad)
  Width = 19.5
FEATURE [Part::Box] Box086  label="Cube070"
  AttacherType = Attacher::AttachEngine3D
  Height = 10
  Length = 10
  Placement = pos=(4,-26,1) rot=(0.205904,-0.974848,-0.085288;0.803573rad)
  Width = 15
FEATURE [Part::Box] Box089  label="Cube073"
  AttacherType = Attacher::AttachEngine3D
  Height = 10
  Length = 10
  Placement = pos=(17,32.0919,9.95) rot=(-0.225436,0.969773,-0.093378;0.807337rad)
  Width = 15
FEATURE [Part::Box] Box090  label="Cube074"
  AttacherType = Attacher::AttachEngine3D
  Height = 10
  Length = 15
  Placement = pos=(30.8481,15.8,2.86019) rot=(0.974848,0.205904,-0.085288;0.803573rad)
  Width = 10
FEATURE [Part::Box] Box091  label="Cube075"
  AttacherType = Attacher::AttachEngine3D
  Height = 10
  Length = 10
  Placement = pos=(7.9081,17,9.95) rot=(-0.450607,0.280623,0.847469;1.65638rad)
  Width = 15
FEATURE [Part::Box] Box092  label="Cube076"
  AttacherType = Attacher::AttachEngine3D
  Height = 10
  Length = 10
  Placement = pos=(23,7.9081,9.95) rot=(-0.381178,-0.08861,0.920245;3.06822rad)
  Width = 15
FEATURE [Part::Box] Box093  label="Cube077"
  AttacherType = Attacher::AttachEngine3D
  Height = 7
  Length = 5
  Width = 40
FEATURE [Part::Box] Box094  label="Cube078"
  AttacherType = Attacher::AttachEngine3D
  Height = 7
  Length = 10
  Placement = pos=(-10,6,0) rot=(0,0,1;0rad)
  Width = 2
FEATURE [Part::Box] Box095  label="Cube079"
  AttacherType = Attacher::AttachEngine3D
  Height = 7
  Length = 10
  Placement = pos=(-10,10,0) rot=(0,0,1;0rad)
  Width = 2
FEATURE [Part::Box] Box096  label="Cube080"
  AttacherType = Attacher::AttachEngine3D
  Height = 7
  Length = 10
  Placement = pos=(-10,25.4,0) rot=(0,0,1;0rad)
  Width = 2
FEATURE [Part::Box] Box097  label="Cube081"
  AttacherType = Attacher::AttachEngine3D
  Height = 7
  Length = 10
  Placement = pos=(-10,34.6,0) rot=(0,0,1;0rad)
  Width = 2
FEATURE [Part::Sphere] Sphere035
  Angle1 = -90
  Angle2 = 90
  Angle3 = 360
  AttacherType = Attacher::AttachEngine3D
  Placement = pos=(-3,6.5,2.5) rot=(0,0,1;0rad)
  Radius = 1.25
FEATURE [Part::Box] Box098  label="Cube082"
  AttacherType = Attacher::AttachEngine3D
  Height = 10
  Length = 13
  Placement = pos=(-10.19,0,-1.19) rot=(0,-1,0;0.785398rad)
  Width = 40
FEATURE [Part::Sphere] Sphere036
  Angle1 = -90
  Angle2 = 90
  Angle3 = 360
  AttacherType = Attacher::AttachEngine3D
  Placement = pos=(-3,11.5,2.5) rot=(0,0,1;0rad)
  Radius = 1.25
FEATURE [Part::Sphere] Sphere037
  Angle1 = -90
  Angle2 = 90
  Angle3 = 360
  AttacherType = Attacher::AttachEngine3D
  Placement = pos=(-3,28,2.5) rot=(0,0,1;0rad)
  Radius = 1.5
FEATURE [Part::Sphere] Sphere038
  Angle1 = -90
  Angle2 = 90
  Angle3 = 360
  AttacherType = Attacher::AttachEngine3D
  Placement = pos=(-3,34,2.5) rot=(0,0,1;0rad)
  Radius = 1.5
FEATURE [Part::MultiFuse] Fusion030
  Shapes = -> [Box093,Box094,Box095,Box096,Box097]
FEATURE [Part::Cut] Cut025
  Base = -> Fusion030
  Tool = -> Box098
FEATURE [Part::MultiFuse] Fusion031
  Shapes = -> [Sphere035,Sphere036,Cut025]
FEATURE [Part::MultiFuse] Fusion032
  Shapes = -> [Sphere038,Sphere037]
FEATURE [Part::Cut] Cut026
  Base = -> Fusion031
  Tool = -> Fusion032
FEATURE [Part::Chamfer] Chamfer009
  Base = -> Cut026
  Edges = 4 edges r=4: [Edge31,Edge37,Edge43,Edge46]
FEATURE [Part::Box] Box099  label="Cube083"
  AttacherType = Attacher::AttachEngine3D
  Height = 7
  Length = 4
  Placement = pos=(-1,5,0) rot=(0,0,1;0rad)
  Width = 1
FEATURE [Part::Box] Box100  label="Cube084"
  AttacherType = Attacher::AttachEngine3D
  Height = 7
  Length = 4
  Placement = pos=(-1,8,0) rot=(0,0,1;0rad)
  Width = 2
FEATURE [Part::Box] Box101  label="Cube085"
  AttacherType = Attacher::AttachEngine3D
  Height = 7
  Length = 4
  Placement = pos=(-1,12,0) rot=(0,0,1;0rad)
  Width = 1
FEATURE [Part::Box] Box102  label="Cube086"
  AttacherType = Attacher::AttachEngine3D
  Height = 7
  Length = 4
  Placement = pos=(-1,24.4,0) rot=(0,0,1;0rad)
  Width = 1
FEATURE [Part::Box] Box103  label="Cube087"
  AttacherType = Attacher::AttachEngine3D
  Height = 7
  Length = 4
  Placement = pos=(-1,36.6,0) rot=(0,0,1;0rad)
  Width = 1
FEATURE [Part::Box] Box104  label="Cube088"
  AttacherType = Attacher::AttachEngine3D
  Height = 7
  Length = 4
  Placement = pos=(-1,27.4,0) rot=(0,0,1;0rad)
  Width = 7.2
FEATURE [Part::MultiFuse] Fusion033
  Shapes = -> [Box104,Box101,Box103,Box100,Box102,Box099]
FEATURE [Part::Cut] Cut027
  Base = -> Chamfer009
  Placement = pos=(-5,40,3) rot=(1,0,0;3.14159rad)
  Tool = -> Fusion033
FEATURE [Part::Box] Box105  label="Cube089"
  AttacherType = Attacher::AttachEngine3D
  Height = 10
  Length = 12
  Placement = pos=(-11,-2,-12) rot=(0,0,1;0rad)
  Width = 44
FEATURE [Part::Cut] Cut028
  Base = -> Cut027
  Tool = -> Box105
FEATURE [Part::Box] Box106  label="Cube090"
  AttacherType = Attacher::AttachEngine3D
  Height = 7
  Length = 10
  Placement = pos=(-10,34.6,0) rot=(0,0,1;0rad)
  Width = 2
FEATURE [Part::Box] Box107  label="Cube091"
  AttacherType = Attacher::AttachEngine3D
  Height = 7
  Length = 5
  Width = 40
FEATURE [Part::Box] Box108  label="Cube092"
  AttacherType = Attacher::AttachEngine3D
  Height = 7
  Length = 10
  Placement = pos=(-10,25.4,0) rot=(0,0,1;0rad)
  Width = 2
FEATURE [Part::Box] Box109  label="Cube093"
  AttacherType = Attacher::AttachEngine3D
  Height = 7
  Length = 10
  Placement = pos=(-10,10,0) rot=(0,0,1;0rad)
  Width = 2
FEATURE [Part::Box] Box110  label="Cube094"
  AttacherType = Attacher::AttachEngine3D
  Height = 7
  Length = 10
  Placement = pos=(-10,6,0) rot=(0,0,1;0rad)
  Width = 2
FEATURE [Part::Sphere] Sphere039
  Angle1 = -90
  Angle2 = 90
  Angle3 = 360
  AttacherType = Attacher::AttachEngine3D
  Placement = pos=(-3,6.5,2.5) rot=(0,0,1;0rad)
  Radius = 1.25
FEATURE [Part::Box] Box111  label="Cube095"
  AttacherType = Attacher::AttachEngine3D
  Height = 10
  Length = 13
  Placement = pos=(-10.19,0,-1.19) rot=(0,-1,0;0.785398rad)
  Width = 40
FEATURE [Part::Sphere] Sphere040
  Angle1 = -90
  Angle2 = 90
  Angle3 = 360
  AttacherType = Attacher::AttachEngine3D
  Placement = pos=(-3,11.5,2.5) rot=(0,0,1;0rad)
  Radius = 1.25
FEATURE [Part::Sphere] Sphere041
  Angle1 = -90
  Angle2 = 90
  Angle3 = 360
  AttacherType = Attacher::AttachEngine3D
  Placement = pos=(-3,28,2.5) rot=(0,0,1;0rad)
  Radius = 1.5
FEATURE [Part::Sphere] Sphere042
  Angle1 = -90
  Angle2 = 90
  Angle3 = 360
  AttacherType = Attacher::AttachEngine3D
  Placement = pos=(-3,34,2.5) rot=(0,0,1;0rad)
  Radius = 1.5
FEATURE [Part::MultiFuse] Fusion034
  Shapes = -> [Box107,Box110,Box109,Box108,Box106]
FEATURE [Part::Cut] Cut029
  Base = -> Fusion034
  Tool = -> Box111
FEATURE [Part::MultiFuse] Fusion035
  Shapes = -> [Sphere039,Sphere040,Cut029]
FEATURE [Part::MultiFuse] Fusion036
  Shapes = -> [Sphere042,Sphere041]
FEATURE [Part::Cut] Cut030
  Base = -> Fusion035
  Tool = -> Fusion036
FEATURE [Part::Chamfer] Chamfer010
  Base = -> Cut030
  Edges = 4 edges r=4: [Edge31,Edge37,Edge43,Edge46]
FEATURE [Part::Box] Box112  label="Cube096"
  AttacherType = Attacher::AttachEngine3D
  Height = 7
  Length = 4
  Placement = pos=(-1,5,0) rot=(0,0,1;0rad)
  Width = 1
FEATURE [Part::Box] Box113  label="Cube097"
  AttacherType = Attacher::AttachEngine3D
  Height = 7
  Length = 4
  Placement = pos=(-1,8,0) rot=(0,0,1;0rad)
  Width = 2
FEATURE [Part::Box] Box114  label="Cube098"
  AttacherType = Attacher::AttachEngine3D
  Height = 7
  Length = 4
  Placement = pos=(-1,12,0) rot=(0,0,1;0rad)
  Width = 1
FEATURE [Part::Box] Box115  label="Cube099"
  AttacherType = Attacher::AttachEngine3D
  Height = 7
  Length = 4
  Placement = pos=(-1,24.4,0) rot=(0,0,1;0rad)
  Width = 1
FEATURE [Part::Box] Box116  label="Cube100"
  AttacherType = Attacher::AttachEngine3D
  Height = 7
  Length = 4
  Placement = pos=(-1,36.6,0) rot=(0,0,1;0rad)
  Width = 1
FEATURE [Part::Box] Box117  label="Cube101"
  AttacherType = Attacher::AttachEngine3D
  Height = 7
  Length = 4
  Placement = pos=(-1,27.4,0) rot=(0,0,1;0rad)
  Width = 7.2
FEATURE [Part::MultiFuse] Fusion037
  Shapes = -> [Box117,Box114,Box116,Box113,Box115,Box112]
FEATURE [Part::Cut] Cut031
  Base = -> Chamfer010
  Placement = pos=(-5,40,3) rot=(1,0,0;3.14159rad)
  Tool = -> Fusion037
FEATURE [Part::Box] Box118  label="Cube102"
  AttacherType = Attacher::AttachEngine3D
  Height = 10
  Length = 12
  Placement = pos=(-11,-2,-12) rot=(0,0,1;0rad)
  Width = 44
FEATURE [Part::Cut] Cut032
  Base = -> Cut031
  Placement = pos=(40,0,0) rot=(0,0,1;1.5708rad)
  Tool = -> Box118
FEATURE [Part::Box] Box119  label="Cube103"
  AttacherType = Attacher::AttachEngine3D
  Height = 7
  Length = 4
  Placement = pos=(-1,12,0) rot=(0,0,1;0rad)
  Width = 1
FEATURE [Part::Box] Box120  label="Cube104"
  AttacherType = Attacher::AttachEngine3D
  Height = 10
  Length = 13
  Placement = pos=(-10.19,0,-1.19) rot=(0,-1,0;0.785398rad)
  Width = 40
FEATURE [Part::Box] Box121  label="Cube105"
  AttacherType = Attacher::AttachEngine3D
  Height = 7
  Length = 4
  Placement = pos=(-1,27.4,0) rot=(0,0,1;0rad)
  Width = 7.2
FEATURE [Part::Box] Box122  label="Cube106"
  AttacherType = Attacher::AttachEngine3D
  Height = 7
  Length = 4
  Placement = pos=(-1,5,0) rot=(0,0,1;0rad)
  Width = 1
FEATURE [Part::Box] Box123  label="Cube107"
  AttacherType = Attacher::AttachEngine3D
  Height = 7
  Length = 10
  Placement = pos=(-10,6,0) rot=(0,0,1;0rad)
  Width = 2
FEATURE [Part::Box] Box124  label="Cube108"
  AttacherType = Attacher::AttachEngine3D
  Height = 10
  Length = 12
  Placement = pos=(-11,-2,-12) rot=(0,0,1;0rad)
  Width = 44
FEATURE [Part::Sphere] Sphere043
  Angle1 = -90
  Angle2 = 90
  Angle3 = 360
  AttacherType = Attacher::AttachEngine3D
  Placement = pos=(-3,6.5,2.5) rot=(0,0,1;0rad)
  Radius = 1.25
FEATURE [Part::Box] Box125  label="Cube109"
  AttacherType = Attacher::AttachEngine3D
  Height = 7
  Length = 10
  Placement = pos=(-10,25.4,0) rot=(0,0,1;0rad)
  Width = 2
FEATURE [Part::Box] Box126  label="Cube110"
  AttacherType = Attacher::AttachEngine3D
  Height = 7
  Length = 10
  Placement = pos=(-10,10,0) rot=(0,0,1;0rad)
  Width = 2
FEATURE [Part::Sphere] Sphere044
  Angle1 = -90
  Angle2 = 90
  Angle3 = 360
  AttacherType = Attacher::AttachEngine3D
  Placement = pos=(-3,28,2.5) rot=(0,0,1;0rad)
  Radius = 1.5
FEATURE [Part::Sphere] Sphere045
  Angle1 = -90
  Angle2 = 90
  Angle3 = 360
  AttacherType = Attacher::AttachEngine3D
  Placement = pos=(-3,11.5,2.5) rot=(0,0,1;0rad)
  Radius = 1.25
FEATURE [Part::Box] Box127  label="Cube111"
  AttacherType = Attacher::AttachEngine3D
  Height = 7
  Length = 4
  Placement = pos=(-1,36.6,0) rot=(0,0,1;0rad)
  Width = 1
FEATURE [Part::Sphere] Sphere046
  Angle1 = -90
  Angle2 = 90
  Angle3 = 360
  AttacherType = Attacher::AttachEngine3D
  Placement = pos=(-3,34,2.5) rot=(0,0,1;0rad)
  Radius = 1.5
FEATURE [Part::MultiFuse] Fusion040
  Shapes = -> [Sphere046,Sphere044]
FEATURE [Part::Box] Box128  label="Cube112"
  AttacherType = Attacher::AttachEngine3D
  Height = 7
  Length = 4
  Placement = pos=(-1,8,0) rot=(0,0,1;0rad)
  Width = 2
FEATURE [Part::Box] Box129  label="Cube113"
  AttacherType = Attacher::AttachEngine3D
  Height = 7
  Length = 10
  Placement = pos=(-10,34.6,0) rot=(0,0,1;0rad)
  Width = 2
FEATURE [Part::Box] Box130  label="Cube114"
  AttacherType = Attacher::AttachEngine3D
  Height = 7
  Length = 4
  Placement = pos=(-1,24.4,0) rot=(0,0,1;0rad)
  Width = 1
FEATURE [Part::MultiFuse] Fusion038
  Shapes = -> [Box121,Box119,Box127,Box128,Box130,Box122]
FEATURE [Part::Box] Box131  label="Cube115"
  AttacherType = Attacher::AttachEngine3D
  Height = 7
  Length = 5
  Width = 40
FEATURE [Part::MultiFuse] Fusion041
  Shapes = -> [Box131,Box123,Box126,Box125,Box129]
FEATURE [Part::Cut] Cut035
  Base = -> Fusion041
  Tool = -> Box120
FEATURE [Part::MultiFuse] Fusion039
  Shapes = -> [Sphere043,Sphere045,Cut035]
FEATURE [Part::Cut] Cut036
  Base = -> Fusion039
  Tool = -> Fusion040
FEATURE [Part::Chamfer] Chamfer011
  Base = -> Cut036
  Edges = 4 edges r=4: [Edge31,Edge37,Edge43,Edge46]
FEATURE [Part::Cut] Cut034
  Base = -> Chamfer011
  Placement = pos=(-5,40,3) rot=(1,0,0;3.14159rad)
  Tool = -> Fusion038
FEATURE [Part::Cut] Cut033
  Base = -> Cut034
  Placement = pos=(40,40,0) rot=(0,0,1;3.14159rad)
  Tool = -> Box124
FEATURE [Part::Sphere] Sphere047
  Angle1 = -90
  Angle2 = 90
  Angle3 = 360
  AttacherType = Attacher::AttachEngine3D
  Placement = pos=(-3,11.5,2.5) rot=(0,0,1;0rad)
  Radius = 1.25
FEATURE [Part::Box] Box132  label="Cube116"
  AttacherType = Attacher::AttachEngine3D
  Height = 7
  Length = 10
  Placement = pos=(-10,6,0) rot=(0,0,1;0rad)
  Width = 2
FEATURE [Part::Box] Box133  label="Cube117"
  AttacherType = Attacher::AttachEngine3D
  Height = 7
  Length = 4
  Placement = pos=(-1,8,0) rot=(0,0,1;0rad)
  Width = 2
FEATURE [Part::Box] Box134  label="Cube118"
  AttacherType = Attacher::AttachEngine3D
  Height = 7
  Length = 10
  Placement = pos=(-10,10,0) rot=(0,0,1;0rad)
  Width = 2
FEATURE [Part::Box] Box135  label="Cube119"
  AttacherType = Attacher::AttachEngine3D
  Height = 10
  Length = 12
  Placement = pos=(-11,-2,-12) rot=(0,0,1;0rad)
  Width = 44
FEATURE [Part::Box] Box136  label="Cube120"
  AttacherType = Attacher::AttachEngine3D
  Height = 7
  Length = 4
  Placement = pos=(-1,5,0) rot=(0,0,1;0rad)
  Width = 1
FEATURE [Part::Sphere] Sphere048
  Angle1 = -90
  Angle2 = 90
  Angle3 = 360
  AttacherType = Attacher::AttachEngine3D
  Placement = pos=(-3,28,2.5) rot=(0,0,1;0rad)
  Radius = 1.5
FEATURE [Part::Sphere] Sphere049
  Angle1 = -90
  Angle2 = 90
  Angle3 = 360
  AttacherType = Attacher::AttachEngine3D
  Placement = pos=(-3,6.5,2.5) rot=(0,0,1;0rad)
  Radius = 1.25
FEATURE [Part::Sphere] Sphere050
  Angle1 = -90
  Angle2 = 90
  Angle3 = 360
  AttacherType = Attacher::AttachEngine3D
  Placement = pos=(-3,34,2.5) rot=(0,0,1;0rad)
  Radius = 1.5
FEATURE [Part::Box] Box137  label="Cube121"
  AttacherType = Attacher::AttachEngine3D
  Height = 7
  Length = 4
  Placement = pos=(-1,12,0) rot=(0,0,1;0rad)
  Width = 1
FEATURE [Part::Box] Box138  label="Cube122"
  AttacherType = Attacher::AttachEngine3D
  Height = 7
  Length = 5
  Width = 40
FEATURE [Part::Box] Box139  label="Cube123"
  AttacherType = Attacher::AttachEngine3D
  Height = 7
  Length = 4
  Placement = pos=(-1,36.6,0) rot=(0,0,1;0rad)
  Width = 1
FEATURE [Part::Box] Box140  label="Cube124"
  AttacherType = Attacher::AttachEngine3D
  Height = 7
  Length = 4
  Placement = pos=(-1,24.4,0) rot=(0,0,1;0rad)
  Width = 1
FEATURE [Part::Box] Box141  label="Cube125"
  AttacherType = Attacher::AttachEngine3D
  Height = 7
  Length = 10
  Placement = pos=(-10,25.4,0) rot=(0,0,1;0rad)
  Width = 2
FEATURE [Part::Box] Box142  label="Cube126"
  AttacherType = Attacher::AttachEngine3D
  Height = 10
  Length = 13
  Placement = pos=(-10.19,0,-1.19) rot=(0,-1,0;0.785398rad)
  Width = 40
FEATURE [Part::Box] Box143  label="Cube127"
  AttacherType = Attacher::AttachEngine3D
  Height = 7
  Length = 10
  Placement = pos=(-10,34.6,0) rot=(0,0,1;0rad)
  Width = 2
FEATURE [Part::MultiFuse] Fusion044
  Shapes = -> [Box138,Box132,Box134,Box141,Box143]
FEATURE [Part::Cut] Cut037
  Base = -> Fusion044
  Tool = -> Box142
FEATURE [Part::MultiFuse] Fusion042
  Shapes = -> [Sphere049,Sphere047,Cut037]
FEATURE [Part::MultiFuse] Fusion045
  Shapes = -> [Sphere050,Sphere048]
FEATURE [Part::Cut] Cut038
  Base = -> Fusion042
  Tool = -> Fusion045
FEATURE [Part::Chamfer] Chamfer012
  Base = -> Cut038
  Edges = 4 edges r=4: [Edge31,Edge37,Edge43,Edge46]
FEATURE [Part::Box] Box144  label="Cube128"
  AttacherType = Attacher::AttachEngine3D
  Height = 7
  Length = 4
  Placement = pos=(-1,27.4,0) rot=(0,0,1;0rad)
  Width = 7.2
FEATURE [Part::MultiFuse] Fusion043
  Shapes = -> [Box144,Box137,Box139,Box133,Box140,Box136]
FEATURE [Part::Cut] Cut040
  Base = -> Chamfer012
  Placement = pos=(-5,40,3) rot=(1,0,0;3.14159rad)
  Tool = -> Fusion043
FEATURE [Part::Cut] Cut039
  Base = -> Cut040
  Placement = pos=(0,40,0) rot=(0,0,-1;1.5708rad)
  Tool = -> Box135
FEATURE [Part::MultiFuse] Fusion048
  Shapes = -> [Box089,Box091,Box090,Box092]
FEATURE [Part::Box] Box145  label="Cube129"
  AttacherType = Attacher::AttachEngine3D
  Height = 15
  Length = 19.5
  Placement = pos=(-9.75,-9.75,-14) rot=(0,0,1;0rad)
  Width = 19.5
FEATURE [Part::Box] Box146  label="Cube130"
  AttacherType = Attacher::AttachEngine3D
  Height = 15
  Length = 19.5
  Placement = pos=(-9.75,-9.75,-3) rot=(0,0,1;0rad)
  Width = 19.5
FEATURE [Part::Chamfer] Chamfer013  label="Octagon"
  Base = -> Box146
  Edges = 4 edges r=4: [Edge1,Edge3,Edge5,Edge7]
FEATURE [Part::Box] Box147  label="Cube131"
  AttacherType = Attacher::AttachEngine3D
  Height = 10
  Length = 24
  Placement = pos=(-12,-12,2.1) rot=(0,0,1;0rad)
  Width = 24
FEATURE [Part::Box] Box148  label="Cube132"
  AttacherType = Attacher::AttachEngine3D
  Height = 14
  Length = 20
  Placement = pos=(-10,-10,0) rot=(0,0,1;0rad)
  Width = 20
FEATURE [Part::Cut] Cut043
  Base = -> Box147
  Tool = -> Box148
FEATURE [Part::Chamfer] Chamfer014  label="Glue Channel"
  Base = -> Cut043
  Edges = 8 edges r=0.95: [Edge4,Edge5,Edge14,Edge16,Edge17,Edge18,Edge19,Edge20]
FEATURE [Part::Cut] Cut047
  Base = -> Cut003
  Tool = -> Chamfer007
FEATURE [Part::Cylinder] Cylinder024
  Angle = 360
  AttacherType = Attacher::AttachEngine3D
  Height = 10
  Placement = pos=(-15,-15,-5) rot=(0,0,1;0rad)
  Radius = 1.7
FEATURE [Part::Cylinder] Cylinder025
  Angle = 360
  AttacherType = Attacher::AttachEngine3D
  Height = 10
  Placement = pos=(15,0,-5) rot=(0,0,1;0rad)
  Radius = 1.7
FEATURE [Part::Cylinder] Cylinder026
  Angle = 360
  AttacherType = Attacher::AttachEngine3D
  Height = 10
  Placement = pos=(-15,15,-5) rot=(0,0,1;0rad)
  Radius = 1.7
FEATURE [Part::MultiFuse] Fusion052  label="Screw Holes to remove ball mags"
  Shapes = -> [Cylinder024,Cylinder025,Cylinder026]
FEATURE [Drawing::FeatureViewAnnotation] Annotation
  Font = Sans
  Rotation = 0
  Scale = 7
  Text = 0.4Added in Holes to Mag plate for removal of magnet
  ViewResult = <g transform="translate(14,23) rotate(0)">\n<text id="Annotation"\n font-family="Sans"\n font-size="7"\n fill="#000000">\n<tspan x="0" dy="1em">0.4Added in Holes to Mag plate for removal of magnet</tspan>\n</text>\n</g>
  Visible = false
  X = 14
  Y = 23
FEATURE [Part::Box] Box149  label="Re-level Edge Clip Block001"
  AttacherType = Attacher::AttachEngine3D
  Height = 10
  Length = 12
  Placement = pos=(-21.5,-2,-7) rot=(0,0,1;0rad)
  Width = 44
FEATURE [Part::Fuse] Fusion  label="Bumps"
  Base = -> Sphere008
  Tool = -> Sphere009
FEATURE [Part::Fuse] Fusion053  label="Holes"
  Base = -> Sphere010
  Tool = -> Sphere011
FEATURE [Part::MultiFuse] Fusion054
  Shapes = -> [Box001,Box002,Box003,Box004,Box005]
FEATURE [Part::Fuse] Fusion055
  Base = -> Fusion
  Tool = -> Fusion054
FEATURE [Part::Cut] Cut
  Base = -> Fusion055
  Tool = -> Fusion053
FEATURE [Part::Cut] Cut056
  Base = -> Cut
  Tool = -> Fusion003
FEATURE [Part::Cut] Cut057
  Base = -> Cut056
  Tool = -> Box013
FEATURE [Part::Cut] Cut058
  Base = -> Cut057
  Tool = -> Box149
FEATURE [Part::Cut] Cut059  label="Edge Clips Master"
  Base = -> Cut058
  Placement = pos=(-20,-20,0) rot=(0,0,1;0rad)
  Tool = -> Box006
FEATURE [Part::Box] Box150  label="Cube133"
  AttacherType = Attacher::AttachEngine3D
  Height = 7
  Length = 5
  Placement = pos=(-5,0,-2) rot=(0,0,1;0rad)
  Width = 40
FEATURE [Part::Box] Box151  label="Cube134"
  AttacherType = Attacher::AttachEngine3D
  Height = 7
  Length = 10
  Placement = pos=(-15,6,-2) rot=(0,0,1;0rad)
  Width = 2
FEATURE [Part::Box] Box152  label="Cube135"
  AttacherType = Attacher::AttachEngine3D
  Height = 7
  Length = 10
  Placement = pos=(-15,10,-2) rot=(0,0,1;0rad)
  Width = 2
FEATURE [Part::Box] Box153  label="Cube136"
  AttacherType = Attacher::AttachEngine3D
  Height = 7
  Length = 10
  Placement = pos=(-15,25.4,-2) rot=(0,0,1;0rad)
  Width = 2
FEATURE [Part::Box] Box154  label="Cube137"
  AttacherType = Attacher::AttachEngine3D
  Height = 7
  Length = 10
  Placement = pos=(-15,34.6,-2) rot=(0,0,1;0rad)
  Width = 2
FEATURE [Part::Sphere] Sphere051
  Angle1 = -90
  Angle2 = 90
  Angle3 = 360
  AttacherType = Attacher::AttachEngine3D
  Placement = pos=(-7.5,6.5,0.5) rot=(0,0,1;0rad)
  Radius = 1.25
FEATURE [Part::Box] Box155  label="Chamfer Cube001"
  AttacherType = Attacher::AttachEngine3D
  Height = 10
  Length = 13
  Placement = pos=(-11.69,0,-1.19) rot=(0,-1,0;0.785398rad)
  Width = 40
FEATURE [Part::Sphere] Sphere052
  Angle1 = -90
  Angle2 = 90
  Angle3 = 360
  AttacherType = Attacher::AttachEngine3D
  Placement = pos=(-7.5,11.5,0.5) rot=(0,0,1;0rad)
  Radius = 1.25
FEATURE [Part::Sphere] Sphere053
  Angle1 = -90
  Angle2 = 90
  Angle3 = 360
  AttacherType = Attacher::AttachEngine3D
  Placement = pos=(-7.5,28,0.5) rot=(0,0,1;0rad)
  Radius = 1.5
FEATURE [Part::Sphere] Sphere054
  Angle1 = -90
  Angle2 = 90
  Angle3 = 360
  AttacherType = Attacher::AttachEngine3D
  Placement = pos=(-7.5,34,0.5) rot=(0,0,1;0rad)
  Radius = 1.5
FEATURE [Part::Box] Box156  label="Cube138"
  AttacherType = Attacher::AttachEngine3D
  Height = 7
  Length = 4
  Placement = pos=(-6,5,-2) rot=(0,0,1;0rad)
  Width = 1
FEATURE [Part::Box] Box157  label="Cube139"
  AttacherType = Attacher::AttachEngine3D
  Height = 7
  Length = 4
  Placement = pos=(-6,8,-2) rot=(0,0,1;0rad)
  Width = 2
FEATURE [Part::Box] Box158  label="Cube140"
  AttacherType = Attacher::AttachEngine3D
  Height = 7
  Length = 4
  Placement = pos=(-6,12,-2) rot=(0,0,1;0rad)
  Width = 1
FEATURE [Part::Box] Box159  label="Cube141"
  AttacherType = Attacher::AttachEngine3D
  Height = 7
  Length = 4
  Placement = pos=(-6,24.4,-2) rot=(0,0,1;0rad)
  Width = 1
FEATURE [Part::Box] Box160  label="Cube142"
  AttacherType = Attacher::AttachEngine3D
  Height = 7
  Length = 4
  Placement = pos=(-6,36.6,-2) rot=(0,0,1;0rad)
  Width = 1
FEATURE [Part::Box] Box161  label="Cube143"
  AttacherType = Attacher::AttachEngine3D
  Height = 7
  Length = 4
  Placement = pos=(-6,27.4,-2) rot=(0,0,1;0rad)
  Width = 7.2
FEATURE [Part::MultiFuse] Fusion056  label="Extra Holes for Clips001"
  Shapes = -> [Box161,Box158,Box160,Box157,Box159,Box156]
FEATURE [Part::Box] Box162  label="Re-level Edge Clip Block002"
  AttacherType = Attacher::AttachEngine3D
  Height = 10
  Length = 20
  Placement = pos=(-19,-2,3) rot=(0,0,1;0rad)
  Width = 44
FEATURE [Part::Box] Box163  label="Re-level Edge Clip Block003"
  AttacherType = Attacher::AttachEngine3D
  Height = 10
  Length = 12
  Placement = pos=(-21.5,-2,-7) rot=(0,0,1;0rad)
  Width = 44
FEATURE [Part::Fuse] Fusion057  label="Bumps001"
  Base = -> Sphere051
  Tool = -> Sphere052
FEATURE [Part::Fuse] Fusion058  label="Holes001"
  Base = -> Sphere053
  Tool = -> Sphere054
FEATURE [Part::MultiFuse] Fusion059
  Shapes = -> [Box150,Box151,Box152,Box153,Box154]
FEATURE [Part::Fuse] Fusion060
  Base = -> Fusion057
  Tool = -> Fusion059
FEATURE [Part::Cut] Cut060
  Base = -> Fusion060
  Tool = -> Fusion058
FEATURE [Part::Cut] Cut061
  Base = -> Cut060
  Tool = -> Fusion056
FEATURE [Part::Cut] Cut062
  Base = -> Cut061
  Tool = -> Box162
FEATURE [Part::Cut] Cut063
  Base = -> Cut062
  Tool = -> Box163
FEATURE [Part::Cut] Cut064  label="Copy Edge Clip"
  Base = -> Cut063
  Placement = pos=(-27,20,-7) rot=(0.707107,0,-0.707107;3.14159rad)
  Tool = -> Box155
FEATURE [App::DocumentObjectGroup] Group001  label="Old"
  Group = -> [Cut008,Cut009,Cut015,Cut018,Fusion021,Fusion023,Group,Cut039,Cut028,Cut032,Cut033,Fusion048]
FEATURE [Part::Box] Box164  label="Cube144"
  AttacherType = Attacher::AttachEngine3D
  Height = 7
  Length = 5
  Placement = pos=(-5,0,-2) rot=(0,0,1;0rad)
  Width = 40
FEATURE [Part::Box] Box165  label="Cube145"
  AttacherType = Attacher::AttachEngine3D
  Height = 7
  Length = 10
  Placement = pos=(-15,6,-2) rot=(0,0,1;0rad)
  Width = 2
FEATURE [Part::Box] Box166  label="Cube146"
  AttacherType = Attacher::AttachEngine3D
  Height = 7
  Length = 10
  Placement = pos=(-15,10,-2) rot=(0,0,1;0rad)
  Width = 2
FEATURE [Part::Box] Box167  label="Cube147"
  AttacherType = Attacher::AttachEngine3D
  Height = 7
  Length = 10
  Placement = pos=(-15,25.4,-2) rot=(0,0,1;0rad)
  Width = 2
FEATURE [Part::Box] Box168  label="Cube148"
  AttacherType = Attacher::AttachEngine3D
  Height = 7
  Length = 10
  Placement = pos=(-15,34.6,-2) rot=(0,0,1;0rad)
  Width = 2
FEATURE [Part::Sphere] Sphere055
  Angle1 = -90
  Angle2 = 90
  Angle3 = 360
  AttacherType = Attacher::AttachEngine3D
  Placement = pos=(-7.5,6.5,0.5) rot=(0,0,1;0rad)
  Radius = 1.25
FEATURE [Part::Box] Box169  label="Chamfer Cube002"
  AttacherType = Attacher::AttachEngine3D
  Height = 10
  Length = 13
  Placement = pos=(-11.69,0,-1.19) rot=(0,-1,0;0.785398rad)
  Width = 40
FEATURE [Part::Sphere] Sphere056
  Angle1 = -90
  Angle2 = 90
  Angle3 = 360
  AttacherType = Attacher::AttachEngine3D
  Placement = pos=(-7.5,11.5,0.5) rot=(0,0,1;0rad)
  Radius = 1.25
FEATURE [Part::Sphere] Sphere057
  Angle1 = -90
  Angle2 = 90
  Angle3 = 360
  AttacherType = Attacher::AttachEngine3D
  Placement = pos=(-7.5,28,0.5) rot=(0,0,1;0rad)
  Radius = 1.5
FEATURE [Part::Sphere] Sphere058
  Angle1 = -90
  Angle2 = 90
  Angle3 = 360
  AttacherType = Attacher::AttachEngine3D
  Placement = pos=(-7.5,34,0.5) rot=(0,0,1;0rad)
  Radius = 1.5
FEATURE [Part::Box] Box170  label="Cube149"
  AttacherType = Attacher::AttachEngine3D
  Height = 7
  Length = 4
  Placement = pos=(-6,5,-2) rot=(0,0,1;0rad)
  Width = 1
FEATURE [Part::Box] Box171  label="Cube150"
  AttacherType = Attacher::AttachEngine3D
  Height = 7
  Length = 4
  Placement = pos=(-6,8,-2) rot=(0,0,1;0rad)
  Width = 2
FEATURE [Part::Box] Box172  label="Cube151"
  AttacherType = Attacher::AttachEngine3D
  Height = 7
  Length = 4
  Placement = pos=(-6,12,-2) rot=(0,0,1;0rad)
  Width = 1
FEATURE [Part::Box] Box173  label="Cube152"
  AttacherType = Attacher::AttachEngine3D
  Height = 7
  Length = 4
  Placement = pos=(-6,24.4,-2) rot=(0,0,1;0rad)
  Width = 1
FEATURE [Part::Box] Box174  label="Cube153"
  AttacherType = Attacher::AttachEngine3D
  Height = 7
  Length = 4
  Placement = pos=(-6,36.6,-2) rot=(0,0,1;0rad)
  Width = 1
FEATURE [Part::Box] Box175  label="Cube154"
  AttacherType = Attacher::AttachEngine3D
  Height = 7
  Length = 4
  Placement = pos=(-6,27.4,-2) rot=(0,0,1;0rad)
  Width = 7.2
FEATURE [Part::MultiFuse] Fusion061  label="Extra Holes for Clips002"
  Shapes = -> [Box175,Box172,Box174,Box171,Box173,Box170]
FEATURE [Part::Box] Box176  label="Re-level Edge Clip Block004"
  AttacherType = Attacher::AttachEngine3D
  Height = 10
  Length = 20
  Placement = pos=(-19,-2,3) rot=(0,0,1;0rad)
  Width = 44
FEATURE [Part::Box] Box177  label="Re-level Edge Clip Block005"
  AttacherType = Attacher::AttachEngine3D
  Height = 10
  Length = 12
  Placement = pos=(-21.5,-2,-7) rot=(0,0,1;0rad)
  Width = 44
FEATURE [Part::Fuse] Fusion062  label="Bumps002"
  Base = -> Sphere055
  Tool = -> Sphere056
FEATURE [Part::Fuse] Fusion063  label="Holes002"
  Base = -> Sphere057
  Tool = -> Sphere058
FEATURE [Part::MultiFuse] Fusion064
  Shapes = -> [Box164,Box165,Box166,Box167,Box168]
FEATURE [Part::Fuse] Fusion065
  Base = -> Fusion062
  Tool = -> Fusion064
FEATURE [Part::Cut] Cut065
  Base = -> Fusion065
  Tool = -> Fusion063
FEATURE [Part::Cut] Cut066
  Base = -> Cut065
  Tool = -> Fusion061
FEATURE [Part::Cut] Cut067
  Base = -> Cut066
  Tool = -> Box176
FEATURE [Part::Cut] Cut068
  Base = -> Cut067
  Tool = -> Box177
FEATURE [Part::Cut] Cut069  label="Edge Clips001"
  Base = -> Cut068
  Placement = pos=(20,-20,0) rot=(0,0,1;1.5708rad)
  Tool = -> Box169
FEATURE [Part::Box] Box178  label="Cube155"
  AttacherType = Attacher::AttachEngine3D
  Height = 7
  Length = 5
  Placement = pos=(-5,0,-2) rot=(0,0,1;0rad)
  Width = 40
FEATURE [Part::Box] Box179  label="Cube156"
  AttacherType = Attacher::AttachEngine3D
  Height = 7
  Length = 10
  Placement = pos=(-15,10,-2) rot=(0,0,1;0rad)
  Width = 2
FEATURE [Part::Box] Box180  label="Re-level Edge Clip Block006"
  AttacherType = Attacher::AttachEngine3D
  Height = 10
  Length = 20
  Placement = pos=(-19,-2,3) rot=(0,0,1;0rad)
  Width = 44
FEATURE [Part::Box] Box181  label="Cube157"
  AttacherType = Attacher::AttachEngine3D
  Height = 7
  Length = 4
  Placement = pos=(-6,27.4,-2) rot=(0,0,1;0rad)
  Width = 7.2
FEATURE [Part::Box] Box182  label="Cube158"
  AttacherType = Attacher::AttachEngine3D
  Height = 7
  Length = 4
  Placement = pos=(-6,12,-2) rot=(0,0,1;0rad)
  Width = 1
FEATURE [Part::Sphere] Sphere059
  Angle1 = -90
  Angle2 = 90
  Angle3 = 360
  AttacherType = Attacher::AttachEngine3D
  Placement = pos=(-7.5,6.5,0.5) rot=(0,0,1;0rad)
  Radius = 1.25
FEATURE [Part::Box] Box183  label="Cube159"
  AttacherType = Attacher::AttachEngine3D
  Height = 7
  Length = 10
  Placement = pos=(-15,25.4,-2) rot=(0,0,1;0rad)
  Width = 2
FEATURE [Part::Box] Box184  label="Cube160"
  AttacherType = Attacher::AttachEngine3D
  Height = 7
  Length = 4
  Placement = pos=(-6,36.6,-2) rot=(0,0,1;0rad)
  Width = 1
FEATURE [Part::Sphere] Sphere060
  Angle1 = -90
  Angle2 = 90
  Angle3 = 360
  AttacherType = Attacher::AttachEngine3D
  Placement = pos=(-7.5,34,0.5) rot=(0,0,1;0rad)
  Radius = 1.5
FEATURE [Part::Box] Box185  label="Cube161"
  AttacherType = Attacher::AttachEngine3D
  Height = 7
  Length = 4
  Placement = pos=(-6,24.4,-2) rot=(0,0,1;0rad)
  Width = 1
FEATURE [Part::Box] Box186  label="Cube162"
  AttacherType = Attacher::AttachEngine3D
  Height = 7
  Length = 4
  Placement = pos=(-6,8,-2) rot=(0,0,1;0rad)
  Width = 2
FEATURE [Part::Box] Box187  label="Re-level Edge Clip Block007"
  AttacherType = Attacher::AttachEngine3D
  Height = 10
  Length = 12
  Placement = pos=(-21.5,-2,-7) rot=(0,0,1;0rad)
  Width = 44
FEATURE [Part::Sphere] Sphere061
  Angle1 = -90
  Angle2 = 90
  Angle3 = 360
  AttacherType = Attacher::AttachEngine3D
  Placement = pos=(-7.5,11.5,0.5) rot=(0,0,1;0rad)
  Radius = 1.25
FEATURE [Part::Sphere] Sphere062
  Angle1 = -90
  Angle2 = 90
  Angle3 = 360
  AttacherType = Attacher::AttachEngine3D
  Placement = pos=(-7.5,28,0.5) rot=(0,0,1;0rad)
  Radius = 1.5
FEATURE [Part::Fuse] Fusion066  label="Holes003"
  Base = -> Sphere062
  Tool = -> Sphere060
FEATURE [Part::Box] Box188  label="Cube163"
  AttacherType = Attacher::AttachEngine3D
  Height = 7
  Length = 10
  Placement = pos=(-15,34.6,-2) rot=(0,0,1;0rad)
  Width = 2
FEATURE [Part::Box] Box189  label="Cube164"
  AttacherType = Attacher::AttachEngine3D
  Height = 7
  Length = 4
  Placement = pos=(-6,5,-2) rot=(0,0,1;0rad)
  Width = 1
FEATURE [Part::MultiFuse] Fusion067  label="Extra Holes for Clips003"
  Shapes = -> [Box181,Box182,Box184,Box186,Box185,Box189]
FEATURE [Part::Box] Box190  label="Cube165"
  AttacherType = Attacher::AttachEngine3D
  Height = 7
  Length = 10
  Placement = pos=(-15,6,-2) rot=(0,0,1;0rad)
  Width = 2
FEATURE [Part::MultiFuse] Fusion069
  Shapes = -> [Box178,Box190,Box179,Box183,Box188]
FEATURE [Part::Fuse] Fusion070  label="Bumps003"
  Base = -> Sphere059
  Tool = -> Sphere061
FEATURE [Part::Fuse] Fusion068
  Base = -> Fusion070
  Tool = -> Fusion069
FEATURE [Part::Cut] Cut073
  Base = -> Fusion068
  Tool = -> Fusion066
FEATURE [Part::Cut] Cut070
  Base = -> Cut073
  Tool = -> Fusion067
FEATURE [Part::Cut] Cut071
  Base = -> Cut070
  Tool = -> Box180
FEATURE [Part::Cut] Cut072
  Base = -> Cut071
  Tool = -> Box187
FEATURE [Part::Box] Box191  label="Chamfer Cube003"
  AttacherType = Attacher::AttachEngine3D
  Height = 10
  Length = 13
  Placement = pos=(-11.69,0,-1.19) rot=(0,-1,0;0.785398rad)
  Width = 40
FEATURE [Part::Cut] Cut074  label="Edge Clips002"
  Base = -> Cut072
  Placement = pos=(20,20,0) rot=(0,0,1;3.14159rad)
  Tool = -> Box191
FEATURE [Part::Box] Box192  label="Cube166"
  AttacherType = Attacher::AttachEngine3D
  Height = 7
  Length = 10
  Placement = pos=(-15,6,-2) rot=(0,0,1;0rad)
  Width = 2
FEATURE [Part::Box] Box193  label="Chamfer Cube004"
  AttacherType = Attacher::AttachEngine3D
  Height = 10
  Length = 13
  Placement = pos=(-11.69,0,-1.19) rot=(0,-1,0;0.785398rad)
  Width = 40
FEATURE [Part::Box] Box194  label="Re-level Edge Clip Block008"
  AttacherType = Attacher::AttachEngine3D
  Height = 10
  Length = 20
  Placement = pos=(-19,-2,3) rot=(0,0,1;0rad)
  Width = 44
FEATURE [Part::Box] Box195  label="Cube167"
  AttacherType = Attacher::AttachEngine3D
  Height = 7
  Length = 10
  Placement = pos=(-15,10,-2) rot=(0,0,1;0rad)
  Width = 2
FEATURE [Part::Box] Box196  label="Cube168"
  AttacherType = Attacher::AttachEngine3D
  Height = 7
  Length = 5
  Placement = pos=(-5,0,-2) rot=(0,0,1;0rad)
  Width = 40
FEATURE [Part::Box] Box197  label="Cube169"
  AttacherType = Attacher::AttachEngine3D
  Height = 7
  Length = 4
  Placement = pos=(-6,5,-2) rot=(0,0,1;0rad)
  Width = 1
FEATURE [Part::Box] Box198  label="Cube170"
  AttacherType = Attacher::AttachEngine3D
  Height = 7
  Length = 4
  Placement = pos=(-6,12,-2) rot=(0,0,1;0rad)
  Width = 1
FEATURE [Part::Box] Box199  label="Cube171"
  AttacherType = Attacher::AttachEngine3D
  Height = 7
  Length = 4
  Placement = pos=(-6,27.4,-2) rot=(0,0,1;0rad)
  Width = 7.2
FEATURE [Part::Box] Box200  label="Cube172"
  AttacherType = Attacher::AttachEngine3D
  Height = 7
  Length = 4
  Placement = pos=(-6,24.4,-2) rot=(0,0,1;0rad)
  Width = 1
FEATURE [Part::Sphere] Sphere063
  Angle1 = -90
  Angle2 = 90
  Angle3 = 360
  AttacherType = Attacher::AttachEngine3D
  Placement = pos=(-7.5,28,0.5) rot=(0,0,1;0rad)
  Radius = 1.5
FEATURE [Part::Sphere] Sphere064
  Angle1 = -90
  Angle2 = 90
  Angle3 = 360
  AttacherType = Attacher::AttachEngine3D
  Placement = pos=(-7.5,11.5,0.5) rot=(0,0,1;0rad)
  Radius = 1.25
FEATURE [Part::Box] Box201  label="Cube173"
  AttacherType = Attacher::AttachEngine3D
  Height = 7
  Length = 4
  Placement = pos=(-6,8,-2) rot=(0,0,1;0rad)
  Width = 2
FEATURE [Part::Box] Box202  label="Cube174"
  AttacherType = Attacher::AttachEngine3D
  Height = 7
  Length = 10
  Placement = pos=(-15,25.4,-2) rot=(0,0,1;0rad)
  Width = 2
FEATURE [Part::Sphere] Sphere065
  Angle1 = -90
  Angle2 = 90
  Angle3 = 360
  AttacherType = Attacher::AttachEngine3D
  Placement = pos=(-7.5,6.5,0.5) rot=(0,0,1;0rad)
  Radius = 1.25
FEATURE [Part::Fuse] Fusion073  label="Bumps004"
  Base = -> Sphere065
  Tool = -> Sphere064
FEATURE [Part::Sphere] Sphere066
  Angle1 = -90
  Angle2 = 90
  Angle3 = 360
  AttacherType = Attacher::AttachEngine3D
  Placement = pos=(-7.5,34,0.5) rot=(0,0,1;0rad)
  Radius = 1.5
FEATURE [Part::Fuse] Fusion071  label="Holes004"
  Base = -> Sphere063
  Tool = -> Sphere066
FEATURE [Part::Box] Box203  label="Re-level Edge Clip Block009"
  AttacherType = Attacher::AttachEngine3D
  Height = 10
  Length = 12
  Placement = pos=(-21.5,-2,-7) rot=(0,0,1;0rad)
  Width = 44
FEATURE [Part::Box] Box204  label="Cube175"
  AttacherType = Attacher::AttachEngine3D
  Height = 7
  Length = 4
  Placement = pos=(-6,36.6,-2) rot=(0,0,1;0rad)
  Width = 1
FEATURE [Part::MultiFuse] Fusion074  label="Extra Holes for Clips004"
  Shapes = -> [Box199,Box198,Box204,Box201,Box200,Box197]
FEATURE [Part::Box] Box205  label="Cube176"
  AttacherType = Attacher::AttachEngine3D
  Height = 7
  Length = 10
  Placement = pos=(-15,34.6,-2) rot=(0,0,1;0rad)
  Width = 2
FEATURE [Part::MultiFuse] Fusion072
  Shapes = -> [Box196,Box192,Box195,Box202,Box205]
FEATURE [Part::Fuse] Fusion075
  Base = -> Fusion073
  Tool = -> Fusion072
FEATURE [Part::Cut] Cut075
  Base = -> Fusion075
  Tool = -> Fusion071
FEATURE [Part::Cut] Cut076
  Base = -> Cut075
  Tool = -> Fusion074
FEATURE [Part::Cut] Cut078
  Base = -> Cut076
  Tool = -> Box194
FEATURE [Part::Cut] Cut077
  Base = -> Cut078
  Tool = -> Box203
FEATURE [Part::Cut] Cut079  label="Edge Clips003"
  Base = -> Cut077
  Placement = pos=(-20,20,0) rot=(0,0,-1;1.5708rad)
  Tool = -> Box193
FEATURE [Part::MultiFuse] Fusion076  label="Edge Clips Fusion"
  Shapes = -> [Cut059,Cut069,Cut074,Cut079]
FEATURE [Part::Box] Box206  label="Cube177"
  AttacherType = Attacher::AttachEngine3D
  Height = 10
  Length = 10
  Placement = pos=(26,4,1) rot=(0.442189,-0.287968,0.849437;1.66134rad)
  Width = 15
FEATURE [Part::Box] Box207  label="Cube178"
  AttacherType = Attacher::AttachEngine3D
  Height = 10
  Length = 10
  Placement = pos=(-4,26,1) rot=(0.381439,0.080566,0.920876;3.07487rad)
  Width = 15
FEATURE [Part::Box] Box208  label="Cube179"
  AttacherType = Attacher::AttachEngine3D
  Height = 10
  Length = 10
  Placement = pos=(-26,-4,1) rot=(-0.273007,-0.419215,-0.865867;1.78566rad)
  Width = 15
FEATURE [Part::MultiFuse] Fusion078  label="Glue Dents"
  Shapes = -> [Box086,Box208,Box207,Box206]
FEATURE [Part::Box] Box209  label="Cube180"
  AttacherType = Attacher::AttachEngine3D
  Height = 7
  Length = 5
  Placement = pos=(-5,0,-2) rot=(0,0,1;0rad)
  Width = 40
FEATURE [Part::Box] Box210  label="Cube181"
  AttacherType = Attacher::AttachEngine3D
  Height = 7
  Length = 10
  Placement = pos=(-15,6,-2) rot=(0,0,1;0rad)
  Width = 2
FEATURE [Part::Box] Box211  label="Cube182"
  AttacherType = Attacher::AttachEngine3D
  Height = 7
  Length = 10
  Placement = pos=(-15,10,-2) rot=(0,0,1;0rad)
  Width = 2
FEATURE [Part::Box] Box212  label="Cube183"
  AttacherType = Attacher::AttachEngine3D
  Height = 7
  Length = 10
  Placement = pos=(-15,25.4,-2) rot=(0,0,1;0rad)
  Width = 2
FEATURE [Part::Box] Box213  label="Cube184"
  AttacherType = Attacher::AttachEngine3D
  Height = 7
  Length = 10
  Placement = pos=(-15,34.6,-2) rot=(0,0,1;0rad)
  Width = 2
FEATURE [Part::Sphere] Sphere067
  Angle1 = -90
  Angle2 = 90
  Angle3 = 360
  AttacherType = Attacher::AttachEngine3D
  Placement = pos=(-7.5,6.5,0.5) rot=(0,0,1;0rad)
  Radius = 1.25
FEATURE [Part::Box] Box214  label="Chamfer Cube005"
  AttacherType = Attacher::AttachEngine3D
  Height = 10
  Length = 13
  Placement = pos=(-11.69,0,-1.19) rot=(0,-1,0;0.785398rad)
  Width = 40
FEATURE [Part::Sphere] Sphere068
  Angle1 = -90
  Angle2 = 90
  Angle3 = 360
  AttacherType = Attacher::AttachEngine3D
  Placement = pos=(-7.5,11.5,0.5) rot=(0,0,1;0rad)
  Radius = 1.25
FEATURE [Part::Sphere] Sphere069
  Angle1 = -90
  Angle2 = 90
  Angle3 = 360
  AttacherType = Attacher::AttachEngine3D
  Placement = pos=(-7.5,28,0.5) rot=(0,0,1;0rad)
  Radius = 1.5
FEATURE [Part::Sphere] Sphere070
  Angle1 = -90
  Angle2 = 90
  Angle3 = 360
  AttacherType = Attacher::AttachEngine3D
  Placement = pos=(-7.5,34,0.5) rot=(0,0,1;0rad)
  Radius = 1.5
FEATURE [Part::Box] Box215  label="Cube185"
  AttacherType = Attacher::AttachEngine3D
  Height = 7
  Length = 4
  Placement = pos=(-6,5,-2) rot=(0,0,1;0rad)
  Width = 1
FEATURE [Part::Box] Box216  label="Cube186"
  AttacherType = Attacher::AttachEngine3D
  Height = 7
  Length = 4
  Placement = pos=(-6,8,-2) rot=(0,0,1;0rad)
  Width = 2
FEATURE [Part::Box] Box217  label="Cube187"
  AttacherType = Attacher::AttachEngine3D
  Height = 7
  Length = 4
  Placement = pos=(-6,12,-2) rot=(0,0,1;0rad)
  Width = 1
FEATURE [Part::Box] Box218  label="Cube188"
  AttacherType = Attacher::AttachEngine3D
  Height = 7
  Length = 4
  Placement = pos=(-6,24.4,-2) rot=(0,0,1;0rad)
  Width = 1
FEATURE [Part::Box] Box219  label="Cube189"
  AttacherType = Attacher::AttachEngine3D
  Height = 7
  Length = 4
  Placement = pos=(-6,36.6,-2) rot=(0,0,1;0rad)
  Width = 1
FEATURE [Part::Box] Box220  label="Cube190"
  AttacherType = Attacher::AttachEngine3D
  Height = 7
  Length = 4
  Placement = pos=(-6,27.4,-2) rot=(0,0,1;0rad)
  Width = 7.2
FEATURE [Part::MultiFuse] Fusion079  label="Extra Holes for Clips005"
  Shapes = -> [Box220,Box217,Box219,Box216,Box218,Box215]
FEATURE [Part::Box] Box221  label="Re-level Edge Clip Block010"
  AttacherType = Attacher::AttachEngine3D
  Height = 10
  Length = 20
  Placement = pos=(-19,-2,3) rot=(0,0,1;0rad)
  Width = 44
FEATURE [Part::Box] Box222  label="Re-level Edge Clip Block011"
  AttacherType = Attacher::AttachEngine3D
  Height = 10
  Length = 12
  Placement = pos=(-21.5,-2,-7) rot=(0,0,1;0rad)
  Width = 44
FEATURE [Part::Fuse] Fusion080  label="Bumps005"
  Base = -> Sphere067
  Tool = -> Sphere068
FEATURE [Part::Fuse] Fusion081  label="Holes005"
  Base = -> Sphere069
  Tool = -> Sphere070
FEATURE [Part::MultiFuse] Fusion082
  Shapes = -> [Box209,Box210,Box211,Box212,Box213]
FEATURE [Part::Fuse] Fusion083
  Base = -> Fusion080
  Tool = -> Fusion082
FEATURE [Part::Cut] Cut082
  Base = -> Fusion083
  Tool = -> Fusion081
FEATURE [Part::Cut] Cut083
  Base = -> Cut082
  Tool = -> Fusion079
FEATURE [Part::Cut] Cut084
  Base = -> Cut083
  Tool = -> Box221
FEATURE [Part::Cut] Cut085
  Base = -> Cut084
  Tool = -> Box222
FEATURE [Part::Cut] Cut086  label="Edge Clips Master001"
  Base = -> Cut085
  Placement = pos=(-20,-20,0) rot=(0,0,1;0rad)
  Tool = -> Box214
FEATURE [Part::Box] Box223  label="Cube191"
  AttacherType = Attacher::AttachEngine3D
  Height = 7
  Length = 5
  Placement = pos=(-5,0,-2) rot=(0,0,1;0rad)
  Width = 40
FEATURE [Part::Box] Box224  label="Cube192"
  AttacherType = Attacher::AttachEngine3D
  Height = 7
  Length = 4
  Placement = pos=(-6,8,-2) rot=(0,0,1;0rad)
  Width = 2
FEATURE [Part::Box] Box225  label="Chamfer Cube006"
  AttacherType = Attacher::AttachEngine3D
  Height = 10
  Length = 13
  Placement = pos=(-11.69,0,-1.19) rot=(0,-1,0;0.785398rad)
  Width = 40
FEATURE [Part::Box] Box226  label="Cube193"
  AttacherType = Attacher::AttachEngine3D
  Height = 7
  Length = 10
  Placement = pos=(-15,6,-2) rot=(0,0,1;0rad)
  Width = 2
FEATURE [Part::Sphere] Sphere071
  Angle1 = -90
  Angle2 = 90
  Angle3 = 360
  AttacherType = Attacher::AttachEngine3D
  Placement = pos=(-7.5,11.5,0.5) rot=(0,0,1;0rad)
  Radius = 1.25
FEATURE [Part::Box] Box227  label="Cube194"
  AttacherType = Attacher::AttachEngine3D
  Height = 7
  Length = 4
  Placement = pos=(-6,27.4,-2) rot=(0,0,1;0rad)
  Width = 7.2
FEATURE [Part::Box] Box228  label="Cube195"
  AttacherType = Attacher::AttachEngine3D
  Height = 7
  Length = 4
  Placement = pos=(-6,12,-2) rot=(0,0,1;0rad)
  Width = 1
FEATURE [Part::Box] Box229  label="Cube196"
  AttacherType = Attacher::AttachEngine3D
  Height = 7
  Length = 4
  Placement = pos=(-6,24.4,-2) rot=(0,0,1;0rad)
  Width = 1
FEATURE [Part::Sphere] Sphere072
  Angle1 = -90
  Angle2 = 90
  Angle3 = 360
  AttacherType = Attacher::AttachEngine3D
  Placement = pos=(-7.5,6.5,0.5) rot=(0,0,1;0rad)
  Radius = 1.25
FEATURE [Part::Box] Box230  label="Cube197"
  AttacherType = Attacher::AttachEngine3D
  Height = 7
  Length = 4
  Placement = pos=(-6,36.6,-2) rot=(0,0,1;0rad)
  Width = 1
FEATURE [Part::Box] Box231  label="Cube198"
  AttacherType = Attacher::AttachEngine3D
  Height = 7
  Length = 10
  Placement = pos=(-15,10,-2) rot=(0,0,1;0rad)
  Width = 2
FEATURE [Part::Sphere] Sphere073
  Angle1 = -90
  Angle2 = 90
  Angle3 = 360
  AttacherType = Attacher::AttachEngine3D
  Placement = pos=(-7.5,34,0.5) rot=(0,0,1;0rad)
  Radius = 1.5
FEATURE [Part::Box] Box232  label="Cube199"
  AttacherType = Attacher::AttachEngine3D
  Height = 7
  Length = 4
  Placement = pos=(-6,5,-2) rot=(0,0,1;0rad)
  Width = 1
FEATURE [Part::MultiFuse] Fusion085  label="Extra Holes for Clips006"
  Shapes = -> [Box227,Box228,Box230,Box224,Box229,Box232]
FEATURE [Part::Box] Box233  label="Re-level Edge Clip Block012"
  AttacherType = Attacher::AttachEngine3D
  Height = 10
  Length = 20
  Placement = pos=(-19,-2,3) rot=(0,0,1;0rad)
  Width = 44
FEATURE [Part::Box] Box234  label="Cube200"
  AttacherType = Attacher::AttachEngine3D
  Height = 7
  Length = 10
  Placement = pos=(-15,34.6,-2) rot=(0,0,1;0rad)
  Width = 2
FEATURE [Part::Box] Box235  label="Cube201"
  AttacherType = Attacher::AttachEngine3D
  Height = 7
  Length = 10
  Placement = pos=(-15,25.4,-2) rot=(0,0,1;0rad)
  Width = 2
FEATURE [Part::MultiFuse] Fusion086
  Shapes = -> [Box223,Box226,Box231,Box235,Box234]
FEATURE [Part::Fuse] Fusion087  label="Bumps006"
  Base = -> Sphere072
  Tool = -> Sphere071
FEATURE [Part::Fuse] Fusion084
  Base = -> Fusion087
  Tool = -> Fusion086
FEATURE [Part::Sphere] Sphere074
  Angle1 = -90
  Angle2 = 90
  Angle3 = 360
  AttacherType = Attacher::AttachEngine3D
  Placement = pos=(-7.5,28,0.5) rot=(0,0,1;0rad)
  Radius = 1.5
FEATURE [Part::Fuse] Fusion088  label="Holes006"
  Base = -> Sphere074
  Tool = -> Sphere073
FEATURE [Part::Box] Box236  label="Re-level Edge Clip Block013"
  AttacherType = Attacher::AttachEngine3D
  Height = 10
  Length = 12
  Placement = pos=(-21.5,-2,-7) rot=(0,0,1;0rad)
  Width = 44
FEATURE [Part::Cut] Cut087
  Base = -> Fusion084
  Tool = -> Fusion088
FEATURE [Part::Cut] Cut088
  Base = -> Cut087
  Tool = -> Fusion085
FEATURE [Part::Cut] Cut089
  Base = -> Cut088
  Tool = -> Box233
FEATURE [Part::Cut] Cut090
  Base = -> Cut089
  Tool = -> Box236
FEATURE [Part::Cut] Cut091  label="Edge Clips004"
  Base = -> Cut090
  Placement = pos=(20,-20,0) rot=(0,0,1;1.5708rad)
  Tool = -> Box225
FEATURE [Part::Box] Box237  label="Re-level Edge Clip Block014"
  AttacherType = Attacher::AttachEngine3D
  Height = 10
  Length = 12
  Placement = pos=(-21.5,-2,-7) rot=(0,0,1;0rad)
  Width = 44
FEATURE [Part::Box] Box238  label="Cube202"
  AttacherType = Attacher::AttachEngine3D
  Height = 7
  Length = 4
  Placement = pos=(-6,36.6,-2) rot=(0,0,1;0rad)
  Width = 1
FEATURE [Part::Box] Box239  label="Cube203"
  AttacherType = Attacher::AttachEngine3D
  Height = 7
  Length = 10
  Placement = pos=(-15,10,-2) rot=(0,0,1;0rad)
  Width = 2
FEATURE [Part::Box] Box240  label="Cube204"
  AttacherType = Attacher::AttachEngine3D
  Height = 7
  Length = 10
  Placement = pos=(-15,25.4,-2) rot=(0,0,1;0rad)
  Width = 2
FEATURE [Part::Box] Box241  label="Re-level Edge Clip Block015"
  AttacherType = Attacher::AttachEngine3D
  Height = 10
  Length = 20
  Placement = pos=(-19,-2,3) rot=(0,0,1;0rad)
  Width = 44
FEATURE [Part::Box] Box242  label="Cube205"
  AttacherType = Attacher::AttachEngine3D
  Height = 7
  Length = 10
  Placement = pos=(-15,34.6,-2) rot=(0,0,1;0rad)
  Width = 2
FEATURE [Part::Sphere] Sphere075
  Angle1 = -90
  Angle2 = 90
  Angle3 = 360
  AttacherType = Attacher::AttachEngine3D
  Placement = pos=(-7.5,34,0.5) rot=(0,0,1;0rad)
  Radius = 1.5
FEATURE [Part::Sphere] Sphere076
  Angle1 = -90
  Angle2 = 90
  Angle3 = 360
  AttacherType = Attacher::AttachEngine3D
  Placement = pos=(-7.5,28,0.5) rot=(0,0,1;0rad)
  Radius = 1.5
FEATURE [Part::Fuse] Fusion089  label="Holes007"
  Base = -> Sphere076
  Tool = -> Sphere075
FEATURE [Part::Box] Box243  label="Cube206"
  AttacherType = Attacher::AttachEngine3D
  Height = 7
  Length = 4
  Placement = pos=(-6,5,-2) rot=(0,0,1;0rad)
  Width = 1
FEATURE [Part::Box] Box244  label="Cube207"
  AttacherType = Attacher::AttachEngine3D
  Height = 7
  Length = 4
  Placement = pos=(-6,24.4,-2) rot=(0,0,1;0rad)
  Width = 1
FEATURE [Part::Sphere] Sphere077
  Angle1 = -90
  Angle2 = 90
  Angle3 = 360
  AttacherType = Attacher::AttachEngine3D
  Placement = pos=(-7.5,11.5,0.5) rot=(0,0,1;0rad)
  Radius = 1.25
FEATURE [Part::Box] Box245  label="Cube208"
  AttacherType = Attacher::AttachEngine3D
  Height = 7
  Length = 4
  Placement = pos=(-6,12,-2) rot=(0,0,1;0rad)
  Width = 1
FEATURE [Part::Box] Box246  label="Chamfer Cube007"
  AttacherType = Attacher::AttachEngine3D
  Height = 10
  Length = 13
  Placement = pos=(-11.69,0,-1.19) rot=(0,-1,0;0.785398rad)
  Width = 40
FEATURE [Part::Sphere] Sphere078
  Angle1 = -90
  Angle2 = 90
  Angle3 = 360
  AttacherType = Attacher::AttachEngine3D
  Placement = pos=(-7.5,6.5,0.5) rot=(0,0,1;0rad)
  Radius = 1.25
FEATURE [Part::Fuse] Fusion090  label="Bumps007"
  Base = -> Sphere078
  Tool = -> Sphere077
FEATURE [Part::Box] Box247  label="Cube209"
  AttacherType = Attacher::AttachEngine3D
  Height = 7
  Length = 5
  Placement = pos=(-5,0,-2) rot=(0,0,1;0rad)
  Width = 40
FEATURE [Part::Box] Box248  label="Cube210"
  AttacherType = Attacher::AttachEngine3D
  Height = 7
  Length = 4
  Placement = pos=(-6,27.4,-2) rot=(0,0,1;0rad)
  Width = 7.2
FEATURE [Part::Box] Box249  label="Cube211"
  AttacherType = Attacher::AttachEngine3D
  Height = 7
  Length = 4
  Placement = pos=(-6,8,-2) rot=(0,0,1;0rad)
  Width = 2
FEATURE [Part::MultiFuse] Fusion091  label="Extra Holes for Clips007"
  Shapes = -> [Box248,Box245,Box238,Box249,Box244,Box243]
FEATURE [Part::Box] Box250  label="Cube212"
  AttacherType = Attacher::AttachEngine3D
  Height = 7
  Length = 10
  Placement = pos=(-15,6,-2) rot=(0,0,1;0rad)
  Width = 2
FEATURE [Part::MultiFuse] Fusion092
  Shapes = -> [Box247,Box250,Box239,Box240,Box242]
FEATURE [Part::Fuse] Fusion093
  Base = -> Fusion090
  Tool = -> Fusion092
FEATURE [Part::Cut] Cut093
  Base = -> Fusion093
  Tool = -> Fusion089
FEATURE [Part::Cut] Cut094
  Base = -> Cut093
  Tool = -> Fusion091
FEATURE [Part::Cut] Cut095
  Base = -> Cut094
  Tool = -> Box241
FEATURE [Part::Cut] Cut096
  Base = -> Cut095
  Tool = -> Box237
FEATURE [Part::Cut] Cut092  label="Edge Clips005"
  Base = -> Cut096
  Placement = pos=(20,20,0) rot=(0,0,1;3.14159rad)
  Tool = -> Box246
FEATURE [Part::Box] Box251  label="Re-level Edge Clip Block016"
  AttacherType = Attacher::AttachEngine3D
  Height = 10
  Length = 12
  Placement = pos=(-21.5,-2,-7) rot=(0,0,1;0rad)
  Width = 44
FEATURE [Part::Box] Box252  label="Cube213"
  AttacherType = Attacher::AttachEngine3D
  Height = 7
  Length = 10
  Placement = pos=(-15,10,-2) rot=(0,0,1;0rad)
  Width = 2
FEATURE [Part::Box] Box253  label="Cube214"
  AttacherType = Attacher::AttachEngine3D
  Height = 7
  Length = 4
  Placement = pos=(-6,12,-2) rot=(0,0,1;0rad)
  Width = 1
FEATURE [Part::Box] Box254  label="Chamfer Cube008"
  AttacherType = Attacher::AttachEngine3D
  Height = 10
  Length = 13
  Placement = pos=(-11.69,0,-1.19) rot=(0,-1,0;0.785398rad)
  Width = 40
FEATURE [Part::Sphere] Sphere079
  Angle1 = -90
  Angle2 = 90
  Angle3 = 360
  AttacherType = Attacher::AttachEngine3D
  Placement = pos=(-7.5,6.5,0.5) rot=(0,0,1;0rad)
  Radius = 1.25
FEATURE [Part::Box] Box255  label="Cube215"
  AttacherType = Attacher::AttachEngine3D
  Height = 7
  Length = 5
  Placement = pos=(-5,0,-2) rot=(0,0,1;0rad)
  Width = 40
FEATURE [Part::Box] Box256  label="Cube216"
  AttacherType = Attacher::AttachEngine3D
  Height = 7
  Length = 4
  Placement = pos=(-6,27.4,-2) rot=(0,0,1;0rad)
  Width = 7.2
FEATURE [Part::Box] Box257  label="Cube217"
  AttacherType = Attacher::AttachEngine3D
  Height = 7
  Length = 4
  Placement = pos=(-6,8,-2) rot=(0,0,1;0rad)
  Width = 2
FEATURE [Part::Box] Box258  label="Cube218"
  AttacherType = Attacher::AttachEngine3D
  Height = 7
  Length = 10
  Placement = pos=(-15,6,-2) rot=(0,0,1;0rad)
  Width = 2
FEATURE [Part::Sphere] Sphere080
  Angle1 = -90
  Angle2 = 90
  Angle3 = 360
  AttacherType = Attacher::AttachEngine3D
  Placement = pos=(-7.5,28,0.5) rot=(0,0,1;0rad)
  Radius = 1.5
FEATURE [Part::Box] Box259  label="Cube219"
  AttacherType = Attacher::AttachEngine3D
  Height = 7
  Length = 4
  Placement = pos=(-6,5,-2) rot=(0,0,1;0rad)
  Width = 1
FEATURE [Part::Box] Box260  label="Cube220"
  AttacherType = Attacher::AttachEngine3D
  Height = 7
  Length = 4
  Placement = pos=(-6,24.4,-2) rot=(0,0,1;0rad)
  Width = 1
FEATURE [Part::Sphere] Sphere081
  Angle1 = -90
  Angle2 = 90
  Angle3 = 360
  AttacherType = Attacher::AttachEngine3D
  Placement = pos=(-7.5,11.5,0.5) rot=(0,0,1;0rad)
  Radius = 1.25
FEATURE [Part::Box] Box261  label="Re-level Edge Clip Block017"
  AttacherType = Attacher::AttachEngine3D
  Height = 10
  Length = 20
  Placement = pos=(-19,-2,3) rot=(0,0,1;0rad)
  Width = 44
FEATURE [Part::Box] Box262  label="Cube221"
  AttacherType = Attacher::AttachEngine3D
  Height = 7
  Length = 10
  Placement = pos=(-15,34.6,-2) rot=(0,0,1;0rad)
  Width = 2
FEATURE [Part::Box] Box263  label="Cube222"
  AttacherType = Attacher::AttachEngine3D
  Height = 7
  Length = 10
  Placement = pos=(-15,25.4,-2) rot=(0,0,1;0rad)
  Width = 2
FEATURE [Part::MultiFuse] Fusion096
  Shapes = -> [Box255,Box258,Box252,Box263,Box262]
FEATURE [Part::Box] Box264  label="Cube223"
  AttacherType = Attacher::AttachEngine3D
  Height = 7
  Length = 4
  Placement = pos=(-6,36.6,-2) rot=(0,0,1;0rad)
  Width = 1
FEATURE [Part::MultiFuse] Fusion095  label="Extra Holes for Clips008"
  Shapes = -> [Box256,Box253,Box264,Box257,Box260,Box259]
FEATURE [Part::Fuse] Fusion098  label="Bumps008"
  Base = -> Sphere079
  Tool = -> Sphere081
FEATURE [Part::Fuse] Fusion094
  Base = -> Fusion098
  Tool = -> Fusion096
FEATURE [Part::Sphere] Sphere082
  Angle1 = -90
  Angle2 = 90
  Angle3 = 360
  AttacherType = Attacher::AttachEngine3D
  Placement = pos=(-7.5,34,0.5) rot=(0,0,1;0rad)
  Radius = 1.5
FEATURE [Part::Fuse] Fusion097  label="Holes008"
  Base = -> Sphere080
  Tool = -> Sphere082
FEATURE [Part::Cut] Cut101
  Base = -> Fusion094
  Tool = -> Fusion097
FEATURE [Part::Cut] Cut097
  Base = -> Cut101
  Tool = -> Fusion095
FEATURE [Part::Cut] Cut098
  Base = -> Cut097
  Tool = -> Box261
FEATURE [Part::Cut] Cut099
  Base = -> Cut098
  Tool = -> Box251
FEATURE [Part::Cut] Cut100  label="Edge Clips006"
  Base = -> Cut099
  Placement = pos=(-20,20,0) rot=(0,0,-1;1.5708rad)
  Tool = -> Box254
FEATURE [Part::Box] Box265  label="Cube224"
  AttacherType = Attacher::AttachEngine3D
  Height = 10
  Length = 10
  Placement = pos=(4,-26,1) rot=(0.205904,-0.974848,-0.085288;0.803573rad)
  Width = 15
FEATURE [Part::Box] Box266  label="Cube225"
  AttacherType = Attacher::AttachEngine3D
  Height = 10
  Length = 10
  Placement = pos=(-26,-4,1) rot=(-0.273007,-0.419215,-0.865867;1.78566rad)
  Width = 15
FEATURE [Part::Box] Box267  label="Cube226"
  AttacherType = Attacher::AttachEngine3D
  Height = 10
  Length = 10
  Placement = pos=(-4,26,1) rot=(0.381439,0.080566,0.920876;3.07487rad)
  Width = 15
FEATURE [Part::Box] Box268  label="Cube227"
  AttacherType = Attacher::AttachEngine3D
  Height = 10
  Length = 10
  Placement = pos=(26,4,1) rot=(0.442189,-0.287968,0.849437;1.66134rad)
  Width = 15
FEATURE [Part::MultiFuse] Fusion099  label="Glue Dents001"
  Shapes = -> [Box265,Box266,Box267,Box268]
FEATURE [Part::MultiFuse] Fusion100  label="Edge Clips Fusion001"
  Shapes = -> [Cut100,Cut086,Cut091,Cut092]
FEATURE [Drawing::FeatureViewAnnotation] Annotation001
  Font = Sans
  Rotation = 0
  Scale = 7
  Text = 0.5 rejigged whole thing, stopped clips overhang and moved bump and holes back 0.5
  ViewResult = <g transform="translate(14,30) rotate(0)">\n<text id="Annotation001"\n font-family="Sans"\n font-size="7"\n fill="#000000">\n<tspan x="0" dy="1em">0.5 rejigged whole thing, stopped clips overhang and moved bump and holes back 0.5</tspan>\n</text>\n</g>
  Visible = false
  X = 14
  Y = 30
FEATURE [Part::Cylinder] Cylinder027
  Angle = 360
  AttacherType = Attacher::AttachEngine3D
  Height = 73
  Placement = pos=(0,0,-50) rot=(0,0,1;0rad)
  Radius = 0.5
FEATURE [Part::MultiFuse] Fusion101
  Placement = pos=(-15,-15,0) rot=(0,0,1;0rad)
  Shapes = -> [Box069,Cylinder018,Sphere030]
FEATURE [App::DocumentObjectGroup] Group002  label="Old 0.1"
  Group = -> [Sphere027,Sphere028,Sphere029,Sphere031,Sphere032,Sphere033,Sphere034,Cylinder012,Cylinder016,Cylinder015,Cylinder014,Cylinder013,Cylinder017,Cylinder019,Box067,Box073,Box071,Box068,Box070,Box072,Box074]
FEATURE [Part::Box] Box269  label="Square Nut Hole 024"
  AttacherType = Attacher::AttachEngine3D
  Height = 2
  Length = 5.8
  Placement = pos=(-2.9,2.9,2.1) rot=(1,0,0;3.14159rad)
  Width = 5.8
FEATURE [Part::Cylinder] Cylinder028
  Angle = 360
  AttacherType = Attacher::AttachEngine3D
  Height = 10
  Placement = pos=(0,0,6.7) rot=(1,0,0;3.14159rad)
  Radius = 1.7
FEATURE [Part::Sphere] Sphere083
  Angle1 = -90
  Angle2 = 90
  Angle3 = 360
  AttacherType = Attacher::AttachEngine3D
  Placement = pos=(0,0,4.3) rot=(1,0,0;3.14159rad)
  Radius = 3.35
FEATURE [Part::MultiFuse] Fusion102
  Placement = pos=(-15,0,0) rot=(0,0,1;0rad)
  Shapes = -> [Box269,Cylinder028,Sphere083]
FEATURE [Part::Fuse] Fusion103
  Base = -> Fusion101
  Tool = -> Fusion102
FEATURE [Part::Feature] Fusion103001
  Placement = pos=(0,0,0) rot=(0,0,1;1.5708rad)
  shape: bbox 21.7 x 6.7 x 10.95 mm, 18 faces, 2 solids (baked)
FEATURE [Part::Feature] Fusion103002
  Placement = pos=(0,0,0) rot=(0,0,1;3.14159rad)
  shape: bbox 6.7 x 21.7 x 10.95 mm, 18 faces, 2 solids (baked)
FEATURE [Part::Feature] Fusion103003
  Placement = pos=(0,0,0) rot=(0,0,-1;1.5708rad)
  shape: bbox 21.7 x 6.7 x 10.95 mm, 18 faces, 2 solids (baked)
FEATURE [Part::MultiFuse] Fusion103004  label="Nut Holes"
  Shapes = -> [Fusion103,Fusion103001,Fusion103002,Fusion103003]
FEATURE [Part::Fuse] Fusion103005  label="Cube with Edge Clips"
  Base = -> Box075
  Tool = -> Fusion100
FEATURE [Part::Cut] Cut102
  Base = -> Fusion103005
  Tool = -> Fusion099
FEATURE [Part::Cut] Cut103
  Base = -> Cut102
  Tool = -> Fusion103004
FEATURE [Part::Cut] Cut104
  Base = -> Cut103
  Tool = -> Chamfer014
FEATURE [Part::Cut] Cut105
  Base = -> Cut104
  Tool = -> Chamfer013
FEATURE [Part::Cut] Cut106  label="Nut Plate 1.1"
  Base = -> Cut105
  Tool = -> Box145
FEATURE [Part::Fuse] Fusion103006
  Base = -> Cut047
  Tool = -> Fusion076
FEATURE [Part::Cut] Cut107
  Base = -> Fusion103006
  Tool = -> Fusion052
FEATURE [Part::Cut] Cut108
  Base = -> Cut107
  Tool = -> Chamfer008
FEATURE [Part::Cut] Cut109
  Base = -> Cut108
  Tool = -> Box085
FEATURE [Part::Cut] Cut110  label="Ball Plate 1.1"
  Base = -> Cut109
  Tool = -> Fusion078
FEATURE [Drawing::FeatureViewAnnotation] Annotation002
  Font = Sans
  Rotation = 0
  Scale = 7
  ViewResult = <g transform="translate(10,10) rotate(0)">\n<text id="Annotation002"\n font-family="Sans"\n font-size="7"\n fill="#000000">\n<tspan x="0" dy="1em"></tspan>\n</text>\n</g>
  Visible = true
  X = 10
  Y = 10
FEATURE [Drawing::FeatureViewAnnotation] Annotation003
  Font = Sans
  Rotation = 0
  Scale = 7
  Text = 0.5 - > 1.0
  ViewResult = <g transform="translate(14,18) rotate(0)">\n<text id="Annotation003"\n font-family="Sans"\n font-size="7"\n fill="#000000">\n<tspan x="0" dy="1em">0.5 - > 1.0</tspan>\n</text>\n</g>
  Visible = true
  X = 14
  Y = 18
FEATURE [Drawing::FeatureViewAnnotation] Annotation004
  Font = Sans
  Rotation = 0
  Scale = 7
  ViewResult = <g transform="translate(10,10) rotate(0)">\n<text id="Annotation004"\n font-family="Sans"\n font-size="7"\n fill="#000000">\n<tspan x="0" dy="1em"></tspan>\n</text>\n</g>
  Visible = true
  X = 10
  Y = 10
FEATURE [Drawing::FeatureViewAnnotation] Annotation005
  Font = Sans
  Rotation = 0
  Scale = 5
  Text = 0.5 is a working version. 1.0 has everything moved to centre point and then the ball and nut holes moved so that blocks can be mounted in half position
  ViewResult = <g transform="translate(10,30) rotate(0)">\n<text id="Annotation005"\n font-family="Sans"\n font-size="5"\n fill="#000000">\n<tspan x="0" dy="1em">0.5 is a working version. 1.0 has everything moved to centre point and then the ball and nut holes moved so that blocks can be mounted in half position</tspan>\n</text>\n</g>
  Visible = true
  X = 10
  Y = 30
FEATURE [Drawing::FeatureViewAnnotation] Annotation006
  Font = Sans
  Rotation = 0
  Scale = 5
  Text = 1.1 Moved the cube creating the hole with the octagon by 1mm to so distance between pcbs is bigger | Also added holes
  ViewResult = <g transform="translate(10,40) rotate(0)">\n<text id="Annotation006"\n font-family="Sans"\n font-size="5"\n fill="#000000">\n<tspan x="0" dy="1em">1.1 Moved the cube creating the hole with the octagon by 1mm to so distance between pcbs is bigger</tspan>\n<tspan x="0" dy="1em">Also added holes</tspan>\n<tspan x="0" dy="1em"></tspan>\n</text>\n</g>
  Visible = true
  X = 10
  Y = 40
FEATURE [Part::Cylinder] Cylinder029
  Angle = 360
  AttacherType = Attacher::AttachEngine3D
  Height = 10
  Placement = pos=(15,-15,-5) rot=(0,0,1;1.5708rad)
  Radius = 1.7
FEATURE [Part::Sphere] Sphere084  label="Mag Hole001"
  Angle1 = -90
  Angle2 = 90
  Angle3 = 360
  AttacherType = Attacher::AttachEngine3D
  Placement = pos=(15,-15,1.7) rot=(0,0,1;1.5708rad)
  Radius = 2.83
FEATURE [Part::Sphere] Sphere085  label="Mag Hole002"
  Angle1 = -90
  Angle2 = 90
  Angle3 = 360
  AttacherType = Attacher::AttachEngine3D
  Placement = pos=(15,15,1.7) rot=(0,0,1;3.14159rad)
  Radius = 2.83
FEATURE [Part::Sphere] Sphere086  label="Mag Hole 004"
  Angle1 = -90
  Angle2 = 90
  Angle3 = 360
  AttacherType = Attacher::AttachEngine3D
  Placement = pos=(0,15,1.7) rot=(0,0,1;1.5708rad)
  Radius = 2.825
FEATURE [Part::Sphere] Sphere087  label="Mag Hole 005"
  Angle1 = -90
  Angle2 = 90
  Angle3 = 360
  AttacherType = Attacher::AttachEngine3D
  Placement = pos=(-15,0,1.7) rot=(0,0,1;3.14159rad)
  Radius = 2.825
FEATURE [Part::Sphere] Sphere088  label="Mag Hole 006"
  Angle1 = -90
  Angle2 = 90
  Angle3 = 360
  AttacherType = Attacher::AttachEngine3D
  Placement = pos=(0,-15,1.7) rot=(0,0,-1;1.5708rad)
  Radius = 2.825
FEATURE [Part::Cylinder] Cylinder030
  Angle = 360
  AttacherType = Attacher::AttachEngine3D
  Height = 10
  Placement = pos=(15,15,-5) rot=(0,0,1;3.14159rad)
  Radius = 1.7
FEATURE [Part::Cylinder] Cylinder031
  Angle = 360
  AttacherType = Attacher::AttachEngine3D
  Height = 10
  Placement = pos=(0,15,-5) rot=(0,0,1;1.5708rad)
  Radius = 1.7
FEATURE [Part::Cylinder] Cylinder032
  Angle = 360
  AttacherType = Attacher::AttachEngine3D
  Height = 10
  Placement = pos=(-15,0,-5) rot=(0,0,1;3.14159rad)
  Radius = 1.7
FEATURE [Part::Cylinder] Cylinder033
  Angle = 360
  AttacherType = Attacher::AttachEngine3D
  Height = 10
  Placement = pos=(0,-15,-5) rot=(0,0,-1;1.5708rad)
  Radius = 1.7
FEATURE [Part::MultiFuse] Fusion103007
  Shapes = -> [Cylinder029,Sphere087,Sphere084,Sphere086,Sphere088,Cylinder032,Cylinder033,Sphere085,Cylinder031,Cylinder030]
FEATURE [Part::Cut] Cut111  label="Ball Plate with Extra Holes"
  Base = -> Cut110
  Tool = -> Fusion103007
FEATURE [Part::Cylinder] Cylinder034
  Angle = 360
  AttacherType = Attacher::AttachEngine3D
  Height = 4
  Placement = pos=(-9.75,-9.75,-3) rot=(0,0,1;0rad)
  Radius = 1.5
FEATURE [Part::Cylinder] Cylinder035
  Angle = 360
  AttacherType = Attacher::AttachEngine3D
  Height = 4
  Placement = pos=(9.75,9.75,-3) rot=(0,0,1;0rad)
  Radius = 1.5
FEATURE [Part::Cylinder] Cylinder036
  Angle = 360
  AttacherType = Attacher::AttachEngine3D
  Height = 4
  Placement = pos=(-9.75,9.75,-3) rot=(0,0,1;0rad)
  Radius = 1.5
FEATURE [Part::Cylinder] Cylinder037
  Angle = 360
  AttacherType = Attacher::AttachEngine3D
  Height = 4
  Placement = pos=(9.75,-9.75,-3) rot=(0,0,1;0rad)
  Radius = 1.5
FEATURE [Part::MultiFuse] Fusion103008
  Shapes = -> [Cylinder034,Cylinder037,Cylinder036,Cylinder035]
FEATURE [Part::Cut] Cut112  label="Ball Plate 1.2"
  Base = -> Cut111
  Tool = -> Fusion103008
FEATURE [Part::Cylinder] Cylinder038
  Angle = 360
  AttacherType = Attacher::AttachEngine3D
  Height = 4
  Placement = pos=(-9.75,-9.75,-3) rot=(0,0,1;0rad)
  Radius = 1.5
FEATURE [Part::Cylinder] Cylinder039
  Angle = 360
  AttacherType = Attacher::AttachEngine3D
  Height = 4
  Placement = pos=(9.75,-9.75,-3) rot=(0,0,1;0rad)
  Radius = 1.5
FEATURE [Part::Cylinder] Cylinder040
  Angle = 360
  AttacherType = Attacher::AttachEngine3D
  Height = 4
  Placement = pos=(-9.75,9.75,-3) rot=(0,0,1;0rad)
  Radius = 1.5
FEATURE [Part::Cylinder] Cylinder041
  Angle = 360
  AttacherType = Attacher::AttachEngine3D
  Height = 4
  Placement = pos=(9.75,9.75,-3) rot=(0,0,1;0rad)
  Radius = 1.5
FEATURE [Part::MultiFuse] Fusion103009
  Shapes = -> [Cylinder038,Cylinder041,Cylinder039,Cylinder040]
FEATURE [Part::Cut] Cut113  label="Nut Plate 1.2"
  Base = -> Cut106
  Tool = -> Fusion103009
FEATURE [Drawing::FeatureViewAnnotation] Annotation007
  Font = Sans
  Rotation = 0
  Scale = 7
  ViewResult = <g transform="translate(10,10) rotate(0)">\n<text id="Annotation007"\n font-family="Sans"\n font-size="7"\n fill="#000000">\n<tspan x="0" dy="1em"></tspan>\n</text>\n</g>
  Visible = true
  X = 10
  Y = 10
FEATURE [Drawing::FeatureViewAnnotation] Annotation008
  Font = Sans
  Rotation = 0
  Scale = 7
  ViewResult = <g transform="translate(10,10) rotate(0)">\n<text id="Annotation008"\n font-family="Sans"\n font-size="7"\n fill="#000000">\n<tspan x="0" dy="1em"></tspan>\n</text>\n</g>
  Visible = true
  X = 10
  Y = 10
FEATURE [Drawing::FeaturePage] Page
  EditableTexts = AUTHOR NAME | CREATION DATE | SUPERVISOR NAME | CHECK DATE | SCALE | WEIGHT | NUMBER | SHEET | TITLE | SUBTITLE
  Group = -> [Annotation,Annotation001,Annotation002,Annotation004,Annotation007,Annotation008]
  Template = <path>
FEATURE [Drawing::FeatureViewAnnotation] Annotation009
  Font = Sans
  Rotation = 0
  Scale = 5
  Text = 1.2 Added holes on the corners of the PCB holes to make it easier to fit
  ViewResult = <g transform="translate(10,50) rotate(0)">\n<text id="Annotation009"\n font-family="Sans"\n font-size="5"\n fill="#000000">\n<tspan x="0" dy="1em">1.1 Moved the cube creating the hole with the octagon by 1mm to so distance between pcbs is bigger</tspan>\n<tspan x="0" dy="1em">Also added holes</tspan>\n<tspan x="0" dy="1em"></tspan>\n</text>\n</g>
  Visible = true
  X = 10
  Y = 50
FEATURE [Drawing::FeaturePage] Page001
  EditableTexts = AUTHOR NAME | CREATION DATE | SUPERVISOR NAME | CHECK DATE | SCALE | WEIGHT | NUMBER | SHEET | TITLE | SUBTITLE
  Group = -> [Annotation003,Annotation005,Annotation006,Annotation009]
  Template = <path>
note: 2 file-system paths scrubbed to <path> (originals preserved in the JSON sidecar)
